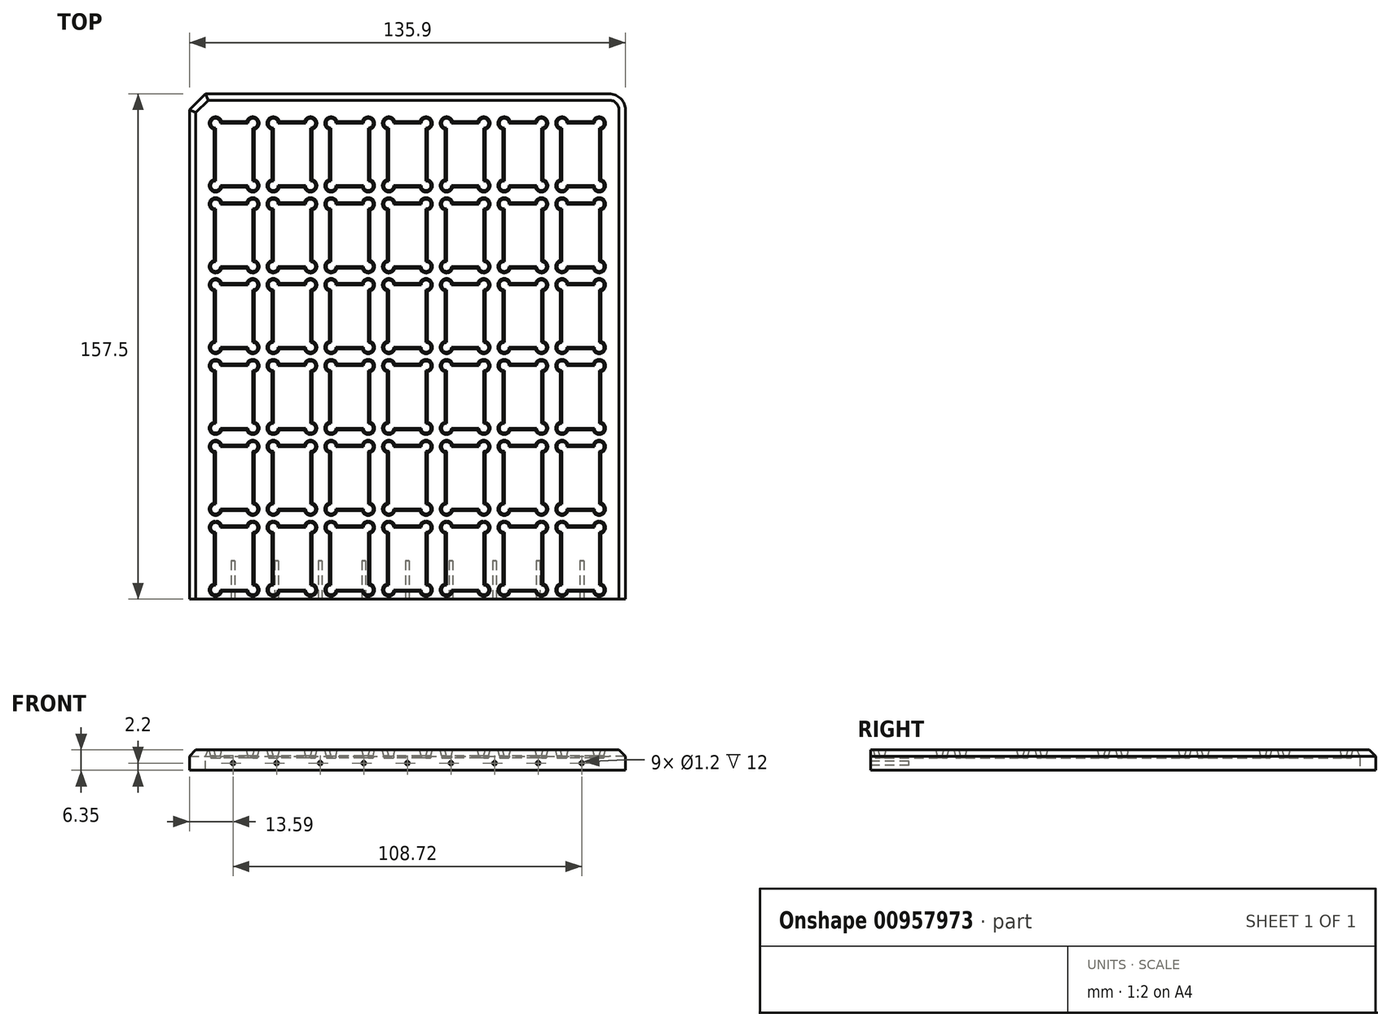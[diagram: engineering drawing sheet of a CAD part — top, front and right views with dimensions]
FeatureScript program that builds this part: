
annotation { "Feature Type Name" : "Feature", "Feature Type Description" : "" }
export const myFeature = defineFeature(function(context is Context, id is Id, definition is map)
    precondition{}
    {
        {
            var Q0;
            Q0=qCreatedBy(makeId("Top.planeOp"),FACE);
            var sketch = newSketch(context, id + "F0", { "sketchPlane" : qUnion([Q0])});
            skLineSegment(sketch, "E0.bottom", {"start": v(0, 0) * mm, "end": v(135.9, 0) * mm});
            skLineSegment(sketch, "E0.top", {"start": v(0, -157.5) * mm, "end": v(135.9, -157.5) * mm});
            skLineSegment(sketch, "E0.left", {"start": v(0, 0) * mm, "end": v(0, -157.5) * mm});
            skLineSegment(sketch, "E0.right", {"start": v(135.9, 0) * mm, "end": v(135.9, -157.5) * mm});
            skSolve(sketch);
        }
        {
            var Q0;
            Q0=makeQuery(id+"F0.imprint","IMPRINT",FACE,{"disambiguationData":[TD([[makeQuery(id+"F0.imprint","IMPRINT",EDGE,{"derivedFrom":sQuery(id+"F0.wireOp",EDGE,"E0.bottom")}),-1.0]])]});
            extrude(context, id + "F1", {"entities" : qUnion([Q0]), "depth" : 3.85 * mm, "offsetDistance" : 25 * mm});
        }
        {
            var Q0;
            Q0=makeQuery(id+"F1.opExtrude","SWEPT_EDGE",EDGE,{"disambiguationData":[OSD([sQuery(id+"F0.wireOp",EDGE,"E0.bottom"),sQuery(id+"F0.wireOp",EDGE,"E0.left")])]});
            chamfer(context, id + "F2", {"entities" : qUnion([Q0]), "chamferType" : ChamferType.OFFSET_ANGLE, "width" : 5 * mm, "oppositeDirection" : false, "angle" : 45 * degree, "tangentPropagation" : true});
        }
        {
            var Q0;
            {var subQ0=sQuery(id+"F0.wireOp",EDGE,"E0.right");var subQ1=sQuery(id+"F0.wireOp",EDGE,"E0.bottom");Q0=makeQuery(id+"F5.boolean.opBoolean","MERGE",EDGE,{"derivedFrom":[makeQuery(id+"F1.opExtrude","SWEPT_EDGE",EDGE,{"disambiguationData":[OSD([subQ1,subQ0])]}),makeQuery(id+"F5.opExtrude","SWEPT_EDGE",EDGE,{"disambiguationData":[OSD([subQ1,subQ0])]})]});}
            fillet(context, id + "F3", {"entities" : qUnion([Q0]), "radius" : 5 * mm, "tangentPropagation" : true, "allowEdgeOverflow" : false});
        }
        {
            var Q0;
            Q0=makeQuery(id+"F1.opExtrude","CAP_FACE",FACE,{"disambiguationData":[OSD([sQuery(id+"F0.wireOp",EDGE,"E0.bottom"),sQuery(id+"F0.wireOp",EDGE,"E0.top"),sQuery(id+"F0.wireOp",EDGE,"E0.left"),sQuery(id+"F0.wireOp",EDGE,"E0.right")])],"isStart":false});
            var sketch = newSketch(context, id + "F4", { "sketchPlane" : qUnion([Q0])});
            skLineSegment(sketch, "E1.bottom", {"start": v(19.75, -28.64) * mm, "end": v(8.15, -28.64) * mm});
            skLineSegment(sketch, "E1.top", {"start": v(19.75, -9.17) * mm, "end": v(8.15, -9.17) * mm});
            skLineSegment(sketch, "E1.left", {"start": v(19.75, -28.64) * mm, "end": v(19.75, -9.17) * mm});
            skLineSegment(sketch, "E1.right", {"start": v(8.15, -28.64) * mm, "end": v(8.15, -9.17) * mm});
            skPoint(sketch, "E1.middle", {"position": v(13.95, -18.9) * mm});
            skCircle(sketch, "E2", {"center": v(8.15, -9.17) * mm, "radius": 1.5 * mm});
            skCircle(sketch, "E3", {"center": v(19.75, -9.17) * mm, "radius": 1.5 * mm});
            skCircle(sketch, "E4", {"center": v(19.75, -28.64) * mm, "radius": 1.5 * mm});
            skCircle(sketch, "E5", {"center": v(8.15, -28.64) * mm, "radius": 1.5 * mm});
            skLineSegment(sketch, "E6.0.1.0", {"start": v(19.75, -53.84) * mm, "end": v(8.15, -53.84) * mm});
            skCircle(sketch, "E6.0.1.1", {"center": v(8.15, -53.84) * mm, "radius": 1.5 * mm});
            skLineSegment(sketch, "E6.0.1.2", {"start": v(8.15, -53.84) * mm, "end": v(8.15, -34.37) * mm});
            skCircle(sketch, "E6.0.1.3", {"center": v(8.15, -34.37) * mm, "radius": 1.5 * mm});
            skLineSegment(sketch, "E6.0.1.4", {"start": v(19.75, -34.37) * mm, "end": v(8.15, -34.37) * mm});
            skCircle(sketch, "E6.0.1.5", {"center": v(19.75, -34.37) * mm, "radius": 1.5 * mm});
            skLineSegment(sketch, "E6.0.1.6", {"start": v(19.75, -53.84) * mm, "end": v(19.75, -34.37) * mm});
            skCircle(sketch, "E6.0.1.7", {"center": v(19.75, -53.84) * mm, "radius": 1.5 * mm});
            skLineSegment(sketch, "E6.0.2.0", {"start": v(19.75, -79.04) * mm, "end": v(8.15, -79.04) * mm});
            skCircle(sketch, "E6.0.2.1", {"center": v(8.15, -79.04) * mm, "radius": 1.5 * mm});
            skLineSegment(sketch, "E6.0.2.2", {"start": v(8.15, -79.04) * mm, "end": v(8.15, -59.57) * mm});
            skCircle(sketch, "E6.0.2.3", {"center": v(8.15, -59.57) * mm, "radius": 1.5 * mm});
            skLineSegment(sketch, "E6.0.2.4", {"start": v(19.75, -59.57) * mm, "end": v(8.15, -59.57) * mm});
            skCircle(sketch, "E6.0.2.5", {"center": v(19.75, -59.57) * mm, "radius": 1.5 * mm});
            skLineSegment(sketch, "E6.0.2.6", {"start": v(19.75, -79.04) * mm, "end": v(19.75, -59.57) * mm});
            skCircle(sketch, "E6.0.2.7", {"center": v(19.75, -79.04) * mm, "radius": 1.5 * mm});
            skLineSegment(sketch, "E6.0.3.0", {"start": v(19.75, -104.24) * mm, "end": v(8.15, -104.24) * mm});
            skCircle(sketch, "E6.0.3.1", {"center": v(8.15, -104.24) * mm, "radius": 1.5 * mm});
            skLineSegment(sketch, "E6.0.3.2", {"start": v(8.15, -104.24) * mm, "end": v(8.15, -84.77) * mm});
            skCircle(sketch, "E6.0.3.3", {"center": v(8.15, -84.77) * mm, "radius": 1.5 * mm});
            skLineSegment(sketch, "E6.0.3.4", {"start": v(19.75, -84.77) * mm, "end": v(8.15, -84.77) * mm});
            skCircle(sketch, "E6.0.3.5", {"center": v(19.75, -84.77) * mm, "radius": 1.5 * mm});
            skLineSegment(sketch, "E6.0.3.6", {"start": v(19.75, -104.24) * mm, "end": v(19.75, -84.77) * mm});
            skCircle(sketch, "E6.0.3.7", {"center": v(19.75, -104.24) * mm, "radius": 1.5 * mm});
            skLineSegment(sketch, "E6.0.4.0", {"start": v(19.75, -129.44) * mm, "end": v(8.15, -129.44) * mm});
            skCircle(sketch, "E6.0.4.1", {"center": v(8.15, -129.44) * mm, "radius": 1.5 * mm});
            skLineSegment(sketch, "E6.0.4.2", {"start": v(8.15, -129.44) * mm, "end": v(8.15, -109.97) * mm});
            skCircle(sketch, "E6.0.4.3", {"center": v(8.15, -109.97) * mm, "radius": 1.5 * mm});
            skLineSegment(sketch, "E6.0.4.4", {"start": v(19.75, -109.97) * mm, "end": v(8.15, -109.97) * mm});
            skCircle(sketch, "E6.0.4.5", {"center": v(19.75, -109.97) * mm, "radius": 1.5 * mm});
            skLineSegment(sketch, "E6.0.4.6", {"start": v(19.75, -129.44) * mm, "end": v(19.75, -109.97) * mm});
            skCircle(sketch, "E6.0.4.7", {"center": v(19.75, -129.44) * mm, "radius": 1.5 * mm});
            skLineSegment(sketch, "E6.1.0.0", {"start": v(37.75, -28.64) * mm, "end": v(26.15, -28.64) * mm});
            skCircle(sketch, "E6.1.0.1", {"center": v(26.15, -28.64) * mm, "radius": 1.5 * mm});
            skLineSegment(sketch, "E6.1.0.2", {"start": v(26.15, -28.64) * mm, "end": v(26.15, -9.17) * mm});
            skCircle(sketch, "E6.1.0.3", {"center": v(26.15, -9.17) * mm, "radius": 1.5 * mm});
            skLineSegment(sketch, "E6.1.0.4", {"start": v(37.75, -9.17) * mm, "end": v(26.15, -9.17) * mm});
            skCircle(sketch, "E6.1.0.5", {"center": v(37.75, -9.17) * mm, "radius": 1.5 * mm});
            skLineSegment(sketch, "E6.1.0.6", {"start": v(37.75, -28.64) * mm, "end": v(37.75, -9.17) * mm});
            skCircle(sketch, "E6.1.0.7", {"center": v(37.75, -28.64) * mm, "radius": 1.5 * mm});
            skLineSegment(sketch, "E6.1.1.0", {"start": v(37.75, -53.84) * mm, "end": v(26.15, -53.84) * mm});
            skCircle(sketch, "E6.1.1.1", {"center": v(26.15, -53.84) * mm, "radius": 1.5 * mm});
            skLineSegment(sketch, "E6.1.1.2", {"start": v(26.15, -53.84) * mm, "end": v(26.15, -34.37) * mm});
            skCircle(sketch, "E6.1.1.3", {"center": v(26.15, -34.37) * mm, "radius": 1.5 * mm});
            skLineSegment(sketch, "E6.1.1.4", {"start": v(37.75, -34.37) * mm, "end": v(26.15, -34.37) * mm});
            skCircle(sketch, "E6.1.1.5", {"center": v(37.75, -34.37) * mm, "radius": 1.5 * mm});
            skLineSegment(sketch, "E6.1.1.6", {"start": v(37.75, -53.84) * mm, "end": v(37.75, -34.37) * mm});
            skCircle(sketch, "E6.1.1.7", {"center": v(37.75, -53.84) * mm, "radius": 1.5 * mm});
            skLineSegment(sketch, "E6.1.2.0", {"start": v(37.75, -79.04) * mm, "end": v(26.15, -79.04) * mm});
            skCircle(sketch, "E6.1.2.1", {"center": v(26.15, -79.04) * mm, "radius": 1.5 * mm});
            skLineSegment(sketch, "E6.1.2.2", {"start": v(26.15, -79.04) * mm, "end": v(26.15, -59.57) * mm});
            skCircle(sketch, "E6.1.2.3", {"center": v(26.15, -59.57) * mm, "radius": 1.5 * mm});
            skLineSegment(sketch, "E6.1.2.4", {"start": v(37.75, -59.57) * mm, "end": v(26.15, -59.57) * mm});
            skCircle(sketch, "E6.1.2.5", {"center": v(37.75, -59.57) * mm, "radius": 1.5 * mm});
            skLineSegment(sketch, "E6.1.2.6", {"start": v(37.75, -79.04) * mm, "end": v(37.75, -59.57) * mm});
            skCircle(sketch, "E6.1.2.7", {"center": v(37.75, -79.04) * mm, "radius": 1.5 * mm});
            skLineSegment(sketch, "E6.1.3.0", {"start": v(37.75, -104.24) * mm, "end": v(26.15, -104.24) * mm});
            skCircle(sketch, "E6.1.3.1", {"center": v(26.15, -104.24) * mm, "radius": 1.5 * mm});
            skLineSegment(sketch, "E6.1.3.2", {"start": v(26.15, -104.24) * mm, "end": v(26.15, -84.77) * mm});
            skCircle(sketch, "E6.1.3.3", {"center": v(26.15, -84.77) * mm, "radius": 1.5 * mm});
            skLineSegment(sketch, "E6.1.3.4", {"start": v(37.75, -84.77) * mm, "end": v(26.15, -84.77) * mm});
            skCircle(sketch, "E6.1.3.5", {"center": v(37.75, -84.77) * mm, "radius": 1.5 * mm});
            skLineSegment(sketch, "E6.1.3.6", {"start": v(37.75, -104.24) * mm, "end": v(37.75, -84.77) * mm});
            skCircle(sketch, "E6.1.3.7", {"center": v(37.75, -104.24) * mm, "radius": 1.5 * mm});
            skLineSegment(sketch, "E6.1.4.0", {"start": v(37.75, -129.44) * mm, "end": v(26.15, -129.44) * mm});
            skCircle(sketch, "E6.1.4.1", {"center": v(26.15, -129.44) * mm, "radius": 1.5 * mm});
            skLineSegment(sketch, "E6.1.4.2", {"start": v(26.15, -129.44) * mm, "end": v(26.15, -109.97) * mm});
            skCircle(sketch, "E6.1.4.3", {"center": v(26.15, -109.97) * mm, "radius": 1.5 * mm});
            skLineSegment(sketch, "E6.1.4.4", {"start": v(37.75, -109.97) * mm, "end": v(26.15, -109.97) * mm});
            skCircle(sketch, "E6.1.4.5", {"center": v(37.75, -109.97) * mm, "radius": 1.5 * mm});
            skLineSegment(sketch, "E6.1.4.6", {"start": v(37.75, -129.44) * mm, "end": v(37.75, -109.97) * mm});
            skCircle(sketch, "E6.1.4.7", {"center": v(37.75, -129.44) * mm, "radius": 1.5 * mm});
            skLineSegment(sketch, "E6.2.0.0", {"start": v(55.75, -28.64) * mm, "end": v(44.15, -28.64) * mm});
            skCircle(sketch, "E6.2.0.1", {"center": v(44.15, -28.64) * mm, "radius": 1.5 * mm});
            skLineSegment(sketch, "E6.2.0.2", {"start": v(44.15, -28.64) * mm, "end": v(44.15, -9.17) * mm});
            skCircle(sketch, "E6.2.0.3", {"center": v(44.15, -9.17) * mm, "radius": 1.5 * mm});
            skLineSegment(sketch, "E6.2.0.4", {"start": v(55.75, -9.17) * mm, "end": v(44.15, -9.17) * mm});
            skCircle(sketch, "E6.2.0.5", {"center": v(55.75, -9.17) * mm, "radius": 1.5 * mm});
            skLineSegment(sketch, "E6.2.0.6", {"start": v(55.75, -28.64) * mm, "end": v(55.75, -9.17) * mm});
            skCircle(sketch, "E6.2.0.7", {"center": v(55.75, -28.64) * mm, "radius": 1.5 * mm});
            skLineSegment(sketch, "E6.2.1.0", {"start": v(55.75, -53.84) * mm, "end": v(44.15, -53.84) * mm});
            skCircle(sketch, "E6.2.1.1", {"center": v(44.15, -53.84) * mm, "radius": 1.5 * mm});
            skLineSegment(sketch, "E6.2.1.2", {"start": v(44.15, -53.84) * mm, "end": v(44.15, -34.37) * mm});
            skCircle(sketch, "E6.2.1.3", {"center": v(44.15, -34.37) * mm, "radius": 1.5 * mm});
            skLineSegment(sketch, "E6.2.1.4", {"start": v(55.75, -34.37) * mm, "end": v(44.15, -34.37) * mm});
            skCircle(sketch, "E6.2.1.5", {"center": v(55.75, -34.37) * mm, "radius": 1.5 * mm});
            skLineSegment(sketch, "E6.2.1.6", {"start": v(55.75, -53.84) * mm, "end": v(55.75, -34.37) * mm});
            skCircle(sketch, "E6.2.1.7", {"center": v(55.75, -53.84) * mm, "radius": 1.5 * mm});
            skLineSegment(sketch, "E6.2.2.0", {"start": v(55.75, -79.04) * mm, "end": v(44.15, -79.04) * mm});
            skCircle(sketch, "E6.2.2.1", {"center": v(44.15, -79.04) * mm, "radius": 1.5 * mm});
            skLineSegment(sketch, "E6.2.2.2", {"start": v(44.15, -79.04) * mm, "end": v(44.15, -59.57) * mm});
            skCircle(sketch, "E6.2.2.3", {"center": v(44.15, -59.57) * mm, "radius": 1.5 * mm});
            skLineSegment(sketch, "E6.2.2.4", {"start": v(55.75, -59.57) * mm, "end": v(44.15, -59.57) * mm});
            skCircle(sketch, "E6.2.2.5", {"center": v(55.75, -59.57) * mm, "radius": 1.5 * mm});
            skLineSegment(sketch, "E6.2.2.6", {"start": v(55.75, -79.04) * mm, "end": v(55.75, -59.57) * mm});
            skCircle(sketch, "E6.2.2.7", {"center": v(55.75, -79.04) * mm, "radius": 1.5 * mm});
            skLineSegment(sketch, "E6.2.3.0", {"start": v(55.75, -104.24) * mm, "end": v(44.15, -104.24) * mm});
            skCircle(sketch, "E6.2.3.1", {"center": v(44.15, -104.24) * mm, "radius": 1.5 * mm});
            skLineSegment(sketch, "E6.2.3.2", {"start": v(44.15, -104.24) * mm, "end": v(44.15, -84.77) * mm});
            skCircle(sketch, "E6.2.3.3", {"center": v(44.15, -84.77) * mm, "radius": 1.5 * mm});
            skLineSegment(sketch, "E6.2.3.4", {"start": v(55.75, -84.77) * mm, "end": v(44.15, -84.77) * mm});
            skCircle(sketch, "E6.2.3.5", {"center": v(55.75, -84.77) * mm, "radius": 1.5 * mm});
            skLineSegment(sketch, "E6.2.3.6", {"start": v(55.75, -104.24) * mm, "end": v(55.75, -84.77) * mm});
            skCircle(sketch, "E6.2.3.7", {"center": v(55.75, -104.24) * mm, "radius": 1.5 * mm});
            skLineSegment(sketch, "E6.2.4.0", {"start": v(55.75, -129.44) * mm, "end": v(44.15, -129.44) * mm});
            skCircle(sketch, "E6.2.4.1", {"center": v(44.15, -129.44) * mm, "radius": 1.5 * mm});
            skLineSegment(sketch, "E6.2.4.2", {"start": v(44.15, -129.44) * mm, "end": v(44.15, -109.97) * mm});
            skCircle(sketch, "E6.2.4.3", {"center": v(44.15, -109.97) * mm, "radius": 1.5 * mm});
            skLineSegment(sketch, "E6.2.4.4", {"start": v(55.75, -109.97) * mm, "end": v(44.15, -109.97) * mm});
            skCircle(sketch, "E6.2.4.5", {"center": v(55.75, -109.97) * mm, "radius": 1.5 * mm});
            skLineSegment(sketch, "E6.2.4.6", {"start": v(55.75, -129.44) * mm, "end": v(55.75, -109.97) * mm});
            skCircle(sketch, "E6.2.4.7", {"center": v(55.75, -129.44) * mm, "radius": 1.5 * mm});
            skLineSegment(sketch, "E6.3.0.0", {"start": v(73.75, -28.64) * mm, "end": v(62.15, -28.64) * mm});
            skCircle(sketch, "E6.3.0.1", {"center": v(62.15, -28.64) * mm, "radius": 1.5 * mm});
            skLineSegment(sketch, "E6.3.0.2", {"start": v(62.15, -28.64) * mm, "end": v(62.15, -9.17) * mm});
            skCircle(sketch, "E6.3.0.3", {"center": v(62.15, -9.17) * mm, "radius": 1.5 * mm});
            skLineSegment(sketch, "E6.3.0.4", {"start": v(73.75, -9.17) * mm, "end": v(62.15, -9.17) * mm});
            skCircle(sketch, "E6.3.0.5", {"center": v(73.75, -9.17) * mm, "radius": 1.5 * mm});
            skLineSegment(sketch, "E6.3.0.6", {"start": v(73.75, -28.64) * mm, "end": v(73.75, -9.17) * mm});
            skCircle(sketch, "E6.3.0.7", {"center": v(73.75, -28.64) * mm, "radius": 1.5 * mm});
            skLineSegment(sketch, "E6.3.1.0", {"start": v(73.75, -53.84) * mm, "end": v(62.15, -53.84) * mm});
            skCircle(sketch, "E6.3.1.1", {"center": v(62.15, -53.84) * mm, "radius": 1.5 * mm});
            skLineSegment(sketch, "E6.3.1.2", {"start": v(62.15, -53.84) * mm, "end": v(62.15, -34.37) * mm});
            skCircle(sketch, "E6.3.1.3", {"center": v(62.15, -34.37) * mm, "radius": 1.5 * mm});
            skLineSegment(sketch, "E6.3.1.4", {"start": v(73.75, -34.37) * mm, "end": v(62.15, -34.37) * mm});
            skCircle(sketch, "E6.3.1.5", {"center": v(73.75, -34.37) * mm, "radius": 1.5 * mm});
            skLineSegment(sketch, "E6.3.1.6", {"start": v(73.75, -53.84) * mm, "end": v(73.75, -34.37) * mm});
            skCircle(sketch, "E6.3.1.7", {"center": v(73.75, -53.84) * mm, "radius": 1.5 * mm});
            skLineSegment(sketch, "E6.3.2.0", {"start": v(73.75, -79.04) * mm, "end": v(62.15, -79.04) * mm});
            skCircle(sketch, "E6.3.2.1", {"center": v(62.15, -79.04) * mm, "radius": 1.5 * mm});
            skLineSegment(sketch, "E6.3.2.2", {"start": v(62.15, -79.04) * mm, "end": v(62.15, -59.57) * mm});
            skCircle(sketch, "E6.3.2.3", {"center": v(62.15, -59.57) * mm, "radius": 1.5 * mm});
            skLineSegment(sketch, "E6.3.2.4", {"start": v(73.75, -59.57) * mm, "end": v(62.15, -59.57) * mm});
            skCircle(sketch, "E6.3.2.5", {"center": v(73.75, -59.57) * mm, "radius": 1.5 * mm});
            skLineSegment(sketch, "E6.3.2.6", {"start": v(73.75, -79.04) * mm, "end": v(73.75, -59.57) * mm});
            skCircle(sketch, "E6.3.2.7", {"center": v(73.75, -79.04) * mm, "radius": 1.5 * mm});
            skLineSegment(sketch, "E6.3.3.0", {"start": v(73.75, -104.24) * mm, "end": v(62.15, -104.24) * mm});
            skCircle(sketch, "E6.3.3.1", {"center": v(62.15, -104.24) * mm, "radius": 1.5 * mm});
            skLineSegment(sketch, "E6.3.3.2", {"start": v(62.15, -104.24) * mm, "end": v(62.15, -84.77) * mm});
            skCircle(sketch, "E6.3.3.3", {"center": v(62.15, -84.77) * mm, "radius": 1.5 * mm});
            skLineSegment(sketch, "E6.3.3.4", {"start": v(73.75, -84.77) * mm, "end": v(62.15, -84.77) * mm});
            skCircle(sketch, "E6.3.3.5", {"center": v(73.75, -84.77) * mm, "radius": 1.5 * mm});
            skLineSegment(sketch, "E6.3.3.6", {"start": v(73.75, -104.24) * mm, "end": v(73.75, -84.77) * mm});
            skCircle(sketch, "E6.3.3.7", {"center": v(73.75, -104.24) * mm, "radius": 1.5 * mm});
            skLineSegment(sketch, "E6.3.4.0", {"start": v(73.75, -129.44) * mm, "end": v(62.15, -129.44) * mm});
            skCircle(sketch, "E6.3.4.1", {"center": v(62.15, -129.44) * mm, "radius": 1.5 * mm});
            skLineSegment(sketch, "E6.3.4.2", {"start": v(62.15, -129.44) * mm, "end": v(62.15, -109.97) * mm});
            skCircle(sketch, "E6.3.4.3", {"center": v(62.15, -109.97) * mm, "radius": 1.5 * mm});
            skLineSegment(sketch, "E6.3.4.4", {"start": v(73.75, -109.97) * mm, "end": v(62.15, -109.97) * mm});
            skCircle(sketch, "E6.3.4.5", {"center": v(73.75, -109.97) * mm, "radius": 1.5 * mm});
            skLineSegment(sketch, "E6.3.4.6", {"start": v(73.75, -129.44) * mm, "end": v(73.75, -109.97) * mm});
            skCircle(sketch, "E6.3.4.7", {"center": v(73.75, -129.44) * mm, "radius": 1.5 * mm});
            skLineSegment(sketch, "E6.4.0.0", {"start": v(91.75, -28.64) * mm, "end": v(80.15, -28.64) * mm});
            skCircle(sketch, "E6.4.0.1", {"center": v(80.15, -28.64) * mm, "radius": 1.5 * mm});
            skLineSegment(sketch, "E6.4.0.2", {"start": v(80.15, -28.64) * mm, "end": v(80.15, -9.17) * mm});
            skCircle(sketch, "E6.4.0.3", {"center": v(80.15, -9.17) * mm, "radius": 1.5 * mm});
            skLineSegment(sketch, "E6.4.0.4", {"start": v(91.75, -9.17) * mm, "end": v(80.15, -9.17) * mm});
            skCircle(sketch, "E6.4.0.5", {"center": v(91.75, -9.17) * mm, "radius": 1.5 * mm});
            skLineSegment(sketch, "E6.4.0.6", {"start": v(91.75, -28.64) * mm, "end": v(91.75, -9.17) * mm});
            skCircle(sketch, "E6.4.0.7", {"center": v(91.75, -28.64) * mm, "radius": 1.5 * mm});
            skLineSegment(sketch, "E6.4.1.0", {"start": v(91.75, -53.84) * mm, "end": v(80.15, -53.84) * mm});
            skCircle(sketch, "E6.4.1.1", {"center": v(80.15, -53.84) * mm, "radius": 1.5 * mm});
            skLineSegment(sketch, "E6.4.1.2", {"start": v(80.15, -53.84) * mm, "end": v(80.15, -34.37) * mm});
            skCircle(sketch, "E6.4.1.3", {"center": v(80.15, -34.37) * mm, "radius": 1.5 * mm});
            skLineSegment(sketch, "E6.4.1.4", {"start": v(91.75, -34.37) * mm, "end": v(80.15, -34.37) * mm});
            skCircle(sketch, "E6.4.1.5", {"center": v(91.75, -34.37) * mm, "radius": 1.5 * mm});
            skLineSegment(sketch, "E6.4.1.6", {"start": v(91.75, -53.84) * mm, "end": v(91.75, -34.37) * mm});
            skCircle(sketch, "E6.4.1.7", {"center": v(91.75, -53.84) * mm, "radius": 1.5 * mm});
            skLineSegment(sketch, "E6.4.2.0", {"start": v(91.75, -79.04) * mm, "end": v(80.15, -79.04) * mm});
            skCircle(sketch, "E6.4.2.1", {"center": v(80.15, -79.04) * mm, "radius": 1.5 * mm});
            skLineSegment(sketch, "E6.4.2.2", {"start": v(80.15, -79.04) * mm, "end": v(80.15, -59.57) * mm});
            skCircle(sketch, "E6.4.2.3", {"center": v(80.15, -59.57) * mm, "radius": 1.5 * mm});
            skLineSegment(sketch, "E6.4.2.4", {"start": v(91.75, -59.57) * mm, "end": v(80.15, -59.57) * mm});
            skCircle(sketch, "E6.4.2.5", {"center": v(91.75, -59.57) * mm, "radius": 1.5 * mm});
            skLineSegment(sketch, "E6.4.2.6", {"start": v(91.75, -79.04) * mm, "end": v(91.75, -59.57) * mm});
            skCircle(sketch, "E6.4.2.7", {"center": v(91.75, -79.04) * mm, "radius": 1.5 * mm});
            skLineSegment(sketch, "E6.4.3.0", {"start": v(91.75, -104.24) * mm, "end": v(80.15, -104.24) * mm});
            skCircle(sketch, "E6.4.3.1", {"center": v(80.15, -104.24) * mm, "radius": 1.5 * mm});
            skLineSegment(sketch, "E6.4.3.2", {"start": v(80.15, -104.24) * mm, "end": v(80.15, -84.77) * mm});
            skCircle(sketch, "E6.4.3.3", {"center": v(80.15, -84.77) * mm, "radius": 1.5 * mm});
            skLineSegment(sketch, "E6.4.3.4", {"start": v(91.75, -84.77) * mm, "end": v(80.15, -84.77) * mm});
            skCircle(sketch, "E6.4.3.5", {"center": v(91.75, -84.77) * mm, "radius": 1.5 * mm});
            skLineSegment(sketch, "E6.4.3.6", {"start": v(91.75, -104.24) * mm, "end": v(91.75, -84.77) * mm});
            skCircle(sketch, "E6.4.3.7", {"center": v(91.75, -104.24) * mm, "radius": 1.5 * mm});
            skLineSegment(sketch, "E6.4.4.0", {"start": v(91.75, -129.44) * mm, "end": v(80.15, -129.44) * mm});
            skCircle(sketch, "E6.4.4.1", {"center": v(80.15, -129.44) * mm, "radius": 1.5 * mm});
            skLineSegment(sketch, "E6.4.4.2", {"start": v(80.15, -129.44) * mm, "end": v(80.15, -109.97) * mm});
            skCircle(sketch, "E6.4.4.3", {"center": v(80.15, -109.97) * mm, "radius": 1.5 * mm});
            skLineSegment(sketch, "E6.4.4.4", {"start": v(91.75, -109.97) * mm, "end": v(80.15, -109.97) * mm});
            skCircle(sketch, "E6.4.4.5", {"center": v(91.75, -109.97) * mm, "radius": 1.5 * mm});
            skLineSegment(sketch, "E6.4.4.6", {"start": v(91.75, -129.44) * mm, "end": v(91.75, -109.97) * mm});
            skCircle(sketch, "E6.4.4.7", {"center": v(91.75, -129.44) * mm, "radius": 1.5 * mm});
            skLineSegment(sketch, "E6.direction1", {"start": v(8.15, -28.64) * mm, "end": v(26.15, -28.64) * mm, "construction": true});
            skLineSegment(sketch, "E6.direction2", {"start": v(8.15, -28.64) * mm, "end": v(8.15, -53.84) * mm, "construction": true});
            skLineSegment(sketch, "E7.0.5.0", {"start": v(109.75, -28.64) * mm, "end": v(98.15, -28.64) * mm});
            skCircle(sketch, "E7.3.5.0", {"center": v(98.15, -28.64) * mm, "radius": 1.5 * mm});
            skLineSegment(sketch, "E7.5.5.0", {"start": v(98.15, -28.64) * mm, "end": v(98.15, -9.17) * mm});
            skCircle(sketch, "E7.8.5.0", {"center": v(98.15, -9.17) * mm, "radius": 1.5 * mm});
            skLineSegment(sketch, "E7.10.5.0", {"start": v(109.75, -9.17) * mm, "end": v(98.15, -9.17) * mm});
            skCircle(sketch, "E7.13.5.0", {"center": v(109.75, -9.17) * mm, "radius": 1.5 * mm});
            skLineSegment(sketch, "E7.15.5.0", {"start": v(109.75, -28.64) * mm, "end": v(109.75, -9.17) * mm});
            skCircle(sketch, "E7.18.5.0", {"center": v(109.75, -28.64) * mm, "radius": 1.5 * mm});
            skLineSegment(sketch, "E7.0.5.1", {"start": v(109.75, -53.84) * mm, "end": v(98.15, -53.84) * mm});
            skCircle(sketch, "E7.3.5.1", {"center": v(98.15, -53.84) * mm, "radius": 1.5 * mm});
            skLineSegment(sketch, "E7.5.5.1", {"start": v(98.15, -53.84) * mm, "end": v(98.15, -34.37) * mm});
            skCircle(sketch, "E7.8.5.1", {"center": v(98.15, -34.37) * mm, "radius": 1.5 * mm});
            skLineSegment(sketch, "E7.10.5.1", {"start": v(109.75, -34.37) * mm, "end": v(98.15, -34.37) * mm});
            skCircle(sketch, "E7.13.5.1", {"center": v(109.75, -34.37) * mm, "radius": 1.5 * mm});
            skLineSegment(sketch, "E7.15.5.1", {"start": v(109.75, -53.84) * mm, "end": v(109.75, -34.37) * mm});
            skCircle(sketch, "E7.18.5.1", {"center": v(109.75, -53.84) * mm, "radius": 1.5 * mm});
            skLineSegment(sketch, "E7.0.5.2", {"start": v(109.75, -79.04) * mm, "end": v(98.15, -79.04) * mm});
            skCircle(sketch, "E7.3.5.2", {"center": v(98.15, -79.04) * mm, "radius": 1.5 * mm});
            skLineSegment(sketch, "E7.5.5.2", {"start": v(98.15, -79.04) * mm, "end": v(98.15, -59.57) * mm});
            skCircle(sketch, "E7.8.5.2", {"center": v(98.15, -59.57) * mm, "radius": 1.5 * mm});
            skLineSegment(sketch, "E7.10.5.2", {"start": v(109.75, -59.57) * mm, "end": v(98.15, -59.57) * mm});
            skCircle(sketch, "E7.13.5.2", {"center": v(109.75, -59.57) * mm, "radius": 1.5 * mm});
            skLineSegment(sketch, "E7.15.5.2", {"start": v(109.75, -79.04) * mm, "end": v(109.75, -59.57) * mm});
            skCircle(sketch, "E7.18.5.2", {"center": v(109.75, -79.04) * mm, "radius": 1.5 * mm});
            skLineSegment(sketch, "E7.0.5.3", {"start": v(109.75, -104.24) * mm, "end": v(98.15, -104.24) * mm});
            skCircle(sketch, "E7.3.5.3", {"center": v(98.15, -104.24) * mm, "radius": 1.5 * mm});
            skLineSegment(sketch, "E7.5.5.3", {"start": v(98.15, -104.24) * mm, "end": v(98.15, -84.77) * mm});
            skCircle(sketch, "E7.8.5.3", {"center": v(98.15, -84.77) * mm, "radius": 1.5 * mm});
            skLineSegment(sketch, "E7.10.5.3", {"start": v(109.75, -84.77) * mm, "end": v(98.15, -84.77) * mm});
            skCircle(sketch, "E7.13.5.3", {"center": v(109.75, -84.77) * mm, "radius": 1.5 * mm});
            skLineSegment(sketch, "E7.15.5.3", {"start": v(109.75, -104.24) * mm, "end": v(109.75, -84.77) * mm});
            skCircle(sketch, "E7.18.5.3", {"center": v(109.75, -104.24) * mm, "radius": 1.5 * mm});
            skLineSegment(sketch, "E7.0.5.4", {"start": v(109.75, -129.44) * mm, "end": v(98.15, -129.44) * mm});
            skCircle(sketch, "E7.3.5.4", {"center": v(98.15, -129.44) * mm, "radius": 1.5 * mm});
            skLineSegment(sketch, "E7.5.5.4", {"start": v(98.15, -129.44) * mm, "end": v(98.15, -109.97) * mm});
            skCircle(sketch, "E7.8.5.4", {"center": v(98.15, -109.97) * mm, "radius": 1.5 * mm});
            skLineSegment(sketch, "E7.10.5.4", {"start": v(109.75, -109.97) * mm, "end": v(98.15, -109.97) * mm});
            skCircle(sketch, "E7.13.5.4", {"center": v(109.75, -109.97) * mm, "radius": 1.5 * mm});
            skLineSegment(sketch, "E7.15.5.4", {"start": v(109.75, -129.44) * mm, "end": v(109.75, -109.97) * mm});
            skCircle(sketch, "E7.18.5.4", {"center": v(109.75, -129.44) * mm, "radius": 1.5 * mm});
            skLineSegment(sketch, "E7.0.6.0", {"start": v(127.75, -28.64) * mm, "end": v(116.15, -28.64) * mm});
            skCircle(sketch, "E7.3.6.0", {"center": v(116.15, -28.64) * mm, "radius": 1.5 * mm});
            skLineSegment(sketch, "E7.5.6.0", {"start": v(116.15, -28.64) * mm, "end": v(116.15, -9.17) * mm});
            skCircle(sketch, "E7.8.6.0", {"center": v(116.15, -9.17) * mm, "radius": 1.5 * mm});
            skLineSegment(sketch, "E7.10.6.0", {"start": v(127.75, -9.17) * mm, "end": v(116.15, -9.17) * mm});
            skCircle(sketch, "E7.13.6.0", {"center": v(127.75, -9.17) * mm, "radius": 1.5 * mm});
            skLineSegment(sketch, "E7.15.6.0", {"start": v(127.75, -28.64) * mm, "end": v(127.75, -9.17) * mm});
            skCircle(sketch, "E7.18.6.0", {"center": v(127.75, -28.64) * mm, "radius": 1.5 * mm});
            skLineSegment(sketch, "E7.0.6.1", {"start": v(127.75, -53.84) * mm, "end": v(116.15, -53.84) * mm});
            skCircle(sketch, "E7.3.6.1", {"center": v(116.15, -53.84) * mm, "radius": 1.5 * mm});
            skLineSegment(sketch, "E7.5.6.1", {"start": v(116.15, -53.84) * mm, "end": v(116.15, -34.37) * mm});
            skCircle(sketch, "E7.8.6.1", {"center": v(116.15, -34.37) * mm, "radius": 1.5 * mm});
            skLineSegment(sketch, "E7.10.6.1", {"start": v(127.75, -34.37) * mm, "end": v(116.15, -34.37) * mm});
            skCircle(sketch, "E7.13.6.1", {"center": v(127.75, -34.37) * mm, "radius": 1.5 * mm});
            skLineSegment(sketch, "E7.15.6.1", {"start": v(127.75, -53.84) * mm, "end": v(127.75, -34.37) * mm});
            skCircle(sketch, "E7.18.6.1", {"center": v(127.75, -53.84) * mm, "radius": 1.5 * mm});
            skLineSegment(sketch, "E7.0.6.2", {"start": v(127.75, -79.04) * mm, "end": v(116.15, -79.04) * mm});
            skCircle(sketch, "E7.3.6.2", {"center": v(116.15, -79.04) * mm, "radius": 1.5 * mm});
            skLineSegment(sketch, "E7.5.6.2", {"start": v(116.15, -79.04) * mm, "end": v(116.15, -59.57) * mm});
            skCircle(sketch, "E7.8.6.2", {"center": v(116.15, -59.57) * mm, "radius": 1.5 * mm});
            skLineSegment(sketch, "E7.10.6.2", {"start": v(127.75, -59.57) * mm, "end": v(116.15, -59.57) * mm});
            skCircle(sketch, "E7.13.6.2", {"center": v(127.75, -59.57) * mm, "radius": 1.5 * mm});
            skLineSegment(sketch, "E7.15.6.2", {"start": v(127.75, -79.04) * mm, "end": v(127.75, -59.57) * mm});
            skCircle(sketch, "E7.18.6.2", {"center": v(127.75, -79.04) * mm, "radius": 1.5 * mm});
            skLineSegment(sketch, "E7.0.6.3", {"start": v(127.75, -104.24) * mm, "end": v(116.15, -104.24) * mm});
            skCircle(sketch, "E7.3.6.3", {"center": v(116.15, -104.24) * mm, "radius": 1.5 * mm});
            skLineSegment(sketch, "E7.5.6.3", {"start": v(116.15, -104.24) * mm, "end": v(116.15, -84.77) * mm});
            skCircle(sketch, "E7.8.6.3", {"center": v(116.15, -84.77) * mm, "radius": 1.5 * mm});
            skLineSegment(sketch, "E7.10.6.3", {"start": v(127.75, -84.77) * mm, "end": v(116.15, -84.77) * mm});
            skCircle(sketch, "E7.13.6.3", {"center": v(127.75, -84.77) * mm, "radius": 1.5 * mm});
            skLineSegment(sketch, "E7.15.6.3", {"start": v(127.75, -104.24) * mm, "end": v(127.75, -84.77) * mm});
            skCircle(sketch, "E7.18.6.3", {"center": v(127.75, -104.24) * mm, "radius": 1.5 * mm});
            skLineSegment(sketch, "E7.0.6.4", {"start": v(127.75, -129.44) * mm, "end": v(116.15, -129.44) * mm});
            skCircle(sketch, "E7.3.6.4", {"center": v(116.15, -129.44) * mm, "radius": 1.5 * mm});
            skLineSegment(sketch, "E7.5.6.4", {"start": v(116.15, -129.44) * mm, "end": v(116.15, -109.97) * mm});
            skCircle(sketch, "E7.8.6.4", {"center": v(116.15, -109.97) * mm, "radius": 1.5 * mm});
            skLineSegment(sketch, "E7.10.6.4", {"start": v(127.75, -109.97) * mm, "end": v(116.15, -109.97) * mm});
            skCircle(sketch, "E7.13.6.4", {"center": v(127.75, -109.97) * mm, "radius": 1.5 * mm});
            skLineSegment(sketch, "E7.15.6.4", {"start": v(127.75, -129.44) * mm, "end": v(127.75, -109.97) * mm});
            skCircle(sketch, "E7.18.6.4", {"center": v(127.75, -129.44) * mm, "radius": 1.5 * mm});
            skLineSegment(sketch, "E8.0.0.5", {"start": v(19.75, -154.64) * mm, "end": v(8.15, -154.64) * mm});
            skCircle(sketch, "E8.3.0.5", {"center": v(8.15, -154.64) * mm, "radius": 1.5 * mm});
            skLineSegment(sketch, "E8.5.0.5", {"start": v(8.15, -154.64) * mm, "end": v(8.15, -135.17) * mm});
            skCircle(sketch, "E8.8.0.5", {"center": v(8.15, -135.17) * mm, "radius": 1.5 * mm});
            skLineSegment(sketch, "E8.10.0.5", {"start": v(19.75, -135.17) * mm, "end": v(8.15, -135.17) * mm});
            skCircle(sketch, "E8.13.0.5", {"center": v(19.75, -135.17) * mm, "radius": 1.5 * mm});
            skLineSegment(sketch, "E8.15.0.5", {"start": v(19.75, -154.64) * mm, "end": v(19.75, -135.17) * mm});
            skCircle(sketch, "E8.18.0.5", {"center": v(19.75, -154.64) * mm, "radius": 1.5 * mm});
            skLineSegment(sketch, "E8.0.1.5", {"start": v(37.75, -154.64) * mm, "end": v(26.15, -154.64) * mm});
            skCircle(sketch, "E8.3.1.5", {"center": v(26.15, -154.64) * mm, "radius": 1.5 * mm});
            skLineSegment(sketch, "E8.5.1.5", {"start": v(26.15, -154.64) * mm, "end": v(26.15, -135.17) * mm});
            skCircle(sketch, "E8.8.1.5", {"center": v(26.15, -135.17) * mm, "radius": 1.5 * mm});
            skLineSegment(sketch, "E8.10.1.5", {"start": v(37.75, -135.17) * mm, "end": v(26.15, -135.17) * mm});
            skCircle(sketch, "E8.13.1.5", {"center": v(37.75, -135.17) * mm, "radius": 1.5 * mm});
            skLineSegment(sketch, "E8.15.1.5", {"start": v(37.75, -154.64) * mm, "end": v(37.75, -135.17) * mm});
            skCircle(sketch, "E8.18.1.5", {"center": v(37.75, -154.64) * mm, "radius": 1.5 * mm});
            skLineSegment(sketch, "E8.0.2.5", {"start": v(55.75, -154.64) * mm, "end": v(44.15, -154.64) * mm});
            skCircle(sketch, "E8.3.2.5", {"center": v(44.15, -154.64) * mm, "radius": 1.5 * mm});
            skLineSegment(sketch, "E8.5.2.5", {"start": v(44.15, -154.64) * mm, "end": v(44.15, -135.17) * mm});
            skCircle(sketch, "E8.8.2.5", {"center": v(44.15, -135.17) * mm, "radius": 1.5 * mm});
            skLineSegment(sketch, "E8.10.2.5", {"start": v(55.75, -135.17) * mm, "end": v(44.15, -135.17) * mm});
            skCircle(sketch, "E8.13.2.5", {"center": v(55.75, -135.17) * mm, "radius": 1.5 * mm});
            skLineSegment(sketch, "E8.15.2.5", {"start": v(55.75, -154.64) * mm, "end": v(55.75, -135.17) * mm});
            skCircle(sketch, "E8.18.2.5", {"center": v(55.75, -154.64) * mm, "radius": 1.5 * mm});
            skLineSegment(sketch, "E8.0.3.5", {"start": v(73.75, -154.64) * mm, "end": v(62.15, -154.64) * mm});
            skCircle(sketch, "E8.3.3.5", {"center": v(62.15, -154.64) * mm, "radius": 1.5 * mm});
            skLineSegment(sketch, "E8.5.3.5", {"start": v(62.15, -154.64) * mm, "end": v(62.15, -135.17) * mm});
            skCircle(sketch, "E8.8.3.5", {"center": v(62.15, -135.17) * mm, "radius": 1.5 * mm});
            skLineSegment(sketch, "E8.10.3.5", {"start": v(73.75, -135.17) * mm, "end": v(62.15, -135.17) * mm});
            skCircle(sketch, "E8.13.3.5", {"center": v(73.75, -135.17) * mm, "radius": 1.5 * mm});
            skLineSegment(sketch, "E8.15.3.5", {"start": v(73.75, -154.64) * mm, "end": v(73.75, -135.17) * mm});
            skCircle(sketch, "E8.18.3.5", {"center": v(73.75, -154.64) * mm, "radius": 1.5 * mm});
            skLineSegment(sketch, "E8.0.4.5", {"start": v(91.75, -154.64) * mm, "end": v(80.15, -154.64) * mm});
            skCircle(sketch, "E8.3.4.5", {"center": v(80.15, -154.64) * mm, "radius": 1.5 * mm});
            skLineSegment(sketch, "E8.5.4.5", {"start": v(80.15, -154.64) * mm, "end": v(80.15, -135.17) * mm});
            skCircle(sketch, "E8.8.4.5", {"center": v(80.15, -135.17) * mm, "radius": 1.5 * mm});
            skLineSegment(sketch, "E8.10.4.5", {"start": v(91.75, -135.17) * mm, "end": v(80.15, -135.17) * mm});
            skCircle(sketch, "E8.13.4.5", {"center": v(91.75, -135.17) * mm, "radius": 1.5 * mm});
            skLineSegment(sketch, "E8.15.4.5", {"start": v(91.75, -154.64) * mm, "end": v(91.75, -135.17) * mm});
            skCircle(sketch, "E8.18.4.5", {"center": v(91.75, -154.64) * mm, "radius": 1.5 * mm});
            skLineSegment(sketch, "E8.0.5.5", {"start": v(109.75, -154.64) * mm, "end": v(98.15, -154.64) * mm});
            skCircle(sketch, "E8.3.5.5", {"center": v(98.15, -154.64) * mm, "radius": 1.5 * mm});
            skLineSegment(sketch, "E8.5.5.5", {"start": v(98.15, -154.64) * mm, "end": v(98.15, -135.17) * mm});
            skCircle(sketch, "E8.8.5.5", {"center": v(98.15, -135.17) * mm, "radius": 1.5 * mm});
            skLineSegment(sketch, "E8.10.5.5", {"start": v(109.75, -135.17) * mm, "end": v(98.15, -135.17) * mm});
            skCircle(sketch, "E8.13.5.5", {"center": v(109.75, -135.17) * mm, "radius": 1.5 * mm});
            skLineSegment(sketch, "E8.15.5.5", {"start": v(109.75, -154.64) * mm, "end": v(109.75, -135.17) * mm});
            skCircle(sketch, "E8.18.5.5", {"center": v(109.75, -154.64) * mm, "radius": 1.5 * mm});
            skLineSegment(sketch, "E8.0.6.5", {"start": v(127.75, -154.64) * mm, "end": v(116.15, -154.64) * mm});
            skCircle(sketch, "E8.3.6.5", {"center": v(116.15, -154.64) * mm, "radius": 1.5 * mm});
            skLineSegment(sketch, "E8.5.6.5", {"start": v(116.15, -154.64) * mm, "end": v(116.15, -135.17) * mm});
            skCircle(sketch, "E8.8.6.5", {"center": v(116.15, -135.17) * mm, "radius": 1.5 * mm});
            skLineSegment(sketch, "E8.10.6.5", {"start": v(127.75, -135.17) * mm, "end": v(116.15, -135.17) * mm});
            skCircle(sketch, "E8.13.6.5", {"center": v(127.75, -135.17) * mm, "radius": 1.5 * mm});
            skLineSegment(sketch, "E8.15.6.5", {"start": v(127.75, -154.64) * mm, "end": v(127.75, -135.17) * mm});
            skCircle(sketch, "E8.18.6.5", {"center": v(127.75, -154.64) * mm, "radius": 1.5 * mm});
            skSolve(sketch);
        }
        {
            var Q0;
            {var subQ603=sQuery(id+"F0.wireOp",EDGE,"E0.top");Q0=makeQuery(id+"F4.imprint","IMPRINT",FACE,{"disambiguationData":[TD([[makeQuery(id+"F4.imprint","IMPRINT",EDGE,{"derivedFrom":makeQuery(id+"F1.opExtrude","CAP_EDGE",EDGE,{"disambiguationData":[OSD([subQ603])],"isStart":false})}),1.0]])]});}
            extrude(context, id + "F5", {"entities" : qUnion([Q0]), "operationType" : NewBodyOperationType.ADD, "depth" : 2.5 * mm, "offsetDistance" : 25 * mm});
        }
        {
            var Q0;
            {var subQ0=sQuery(id+"F0.wireOp",EDGE,"E0.top");Q0=makeQuery(id+"F5.boolean.opBoolean","MERGE",FACE,{"derivedFrom":[makeQuery(id+"F1.opExtrude","SWEPT_FACE",FACE,{"disambiguationData":[OSD([subQ0])]}),makeQuery(id+"F5.opExtrude","SWEPT_FACE",FACE,{"disambiguationData":[OSD([subQ0])]})]});}
            var sketch = newSketch(context, id + "F6", { "sketchPlane" : qUnion([Q0])});
            skCircle(sketch, "E9", {"center": v(13.6, 2.2) * mm, "radius": 0.6 * mm});
            skCircle(sketch, "E10.1.0.0", {"center": v(27.18, 2.2) * mm, "radius": 0.6 * mm});
            skCircle(sketch, "E10.2.0.0", {"center": v(40.77, 2.2) * mm, "radius": 0.6 * mm});
            skCircle(sketch, "E10.3.0.0", {"center": v(54.36, 2.2) * mm, "radius": 0.6 * mm});
            skCircle(sketch, "E10.4.0.0", {"center": v(67.95, 2.2) * mm, "radius": 0.6 * mm});
            skCircle(sketch, "E10.5.0.0", {"center": v(81.54, 2.2) * mm, "radius": 0.6 * mm});
            skCircle(sketch, "E10.6.0.0", {"center": v(95.13, 2.2) * mm, "radius": 0.6 * mm});
            skCircle(sketch, "E10.7.0.0", {"center": v(108.72, 2.2) * mm, "radius": 0.6 * mm});
            skCircle(sketch, "E10.8.0.0", {"center": v(122.31, 2.2) * mm, "radius": 0.6 * mm});
            skLineSegment(sketch, "E10.direction1", {"start": v(27.18, 2.2) * mm, "end": v(40.77, 2.2) * mm, "construction": true});
            skSolve(sketch);
        }
        {
            var Q0;
            Q0=makeQuery(id+"F6.imprint","IMPRINT",FACE,{"disambiguationData":[TD([[makeQuery(id+"F6.imprint","IMPRINT",EDGE,{"derivedFrom":sQuery(id+"F6.wireOp",EDGE,"E9")}),1.0]])]});
            var Q1;
            Q1=makeQuery(id+"F6.imprint","IMPRINT",FACE,{"disambiguationData":[TD([[makeQuery(id+"F6.imprint","IMPRINT",EDGE,{"derivedFrom":sQuery(id+"F6.wireOp",EDGE,"E10.1.0.0")}),1.0]])]});
            var Q2;
            Q2=makeQuery(id+"F6.imprint","IMPRINT",FACE,{"disambiguationData":[TD([[makeQuery(id+"F6.imprint","IMPRINT",EDGE,{"derivedFrom":sQuery(id+"F6.wireOp",EDGE,"E10.2.0.0")}),1.0]])]});
            var Q3;
            Q3=makeQuery(id+"F6.imprint","IMPRINT",FACE,{"disambiguationData":[TD([[makeQuery(id+"F6.imprint","IMPRINT",EDGE,{"derivedFrom":sQuery(id+"F6.wireOp",EDGE,"E10.3.0.0")}),1.0]])]});
            var Q4;
            Q4=makeQuery(id+"F6.imprint","IMPRINT",FACE,{"disambiguationData":[TD([[makeQuery(id+"F6.imprint","IMPRINT",EDGE,{"derivedFrom":sQuery(id+"F6.wireOp",EDGE,"E10.4.0.0")}),1.0]])]});
            var Q5;
            Q5=makeQuery(id+"F6.imprint","IMPRINT",FACE,{"disambiguationData":[TD([[makeQuery(id+"F6.imprint","IMPRINT",EDGE,{"derivedFrom":sQuery(id+"F6.wireOp",EDGE,"E10.5.0.0")}),1.0]])]});
            var Q6;
            Q6=makeQuery(id+"F6.imprint","IMPRINT",FACE,{"disambiguationData":[TD([[makeQuery(id+"F6.imprint","IMPRINT",EDGE,{"derivedFrom":sQuery(id+"F6.wireOp",EDGE,"E10.6.0.0")}),1.0]])]});
            var Q7;
            Q7=makeQuery(id+"F6.imprint","IMPRINT",FACE,{"disambiguationData":[TD([[makeQuery(id+"F6.imprint","IMPRINT",EDGE,{"derivedFrom":sQuery(id+"F6.wireOp",EDGE,"E10.7.0.0")}),1.0]])]});
            var Q8;
            Q8=makeQuery(id+"F6.imprint","IMPRINT",FACE,{"disambiguationData":[TD([[makeQuery(id+"F6.imprint","IMPRINT",EDGE,{"derivedFrom":sQuery(id+"F6.wireOp",EDGE,"E10.8.0.0")}),1.0]])]});
            var Q9;
            Q9=sQuery(id+"F6.wireOp",EDGE,"E9");
            var Q10;
            Q10=sQuery(id+"F6.wireOp",EDGE,"E10.1.0.0");
            var Q11;
            Q11=sQuery(id+"F6.wireOp",EDGE,"E10.2.0.0");
            var Q12;
            Q12=sQuery(id+"F6.wireOp",EDGE,"E10.3.0.0");
            var Q13;
            Q13=sQuery(id+"F6.wireOp",EDGE,"E10.4.0.0");
            var Q14;
            Q14=sQuery(id+"F6.wireOp",EDGE,"E10.5.0.0");
            extrude(context, id + "F7", {"entities" : qUnion([Q0, Q1, Q2, Q3, Q4, Q5, Q6, Q7, Q8]), "operationType" : NewBodyOperationType.REMOVE, "surfaceEntities" : qUnion([Q9, Q10, Q11, Q12, Q13, Q14]), "oppositeDirection" : true, "depth" : 12 * mm, "offsetDistance" : 25 * mm});
        }
        {
            var Q0;
            Q0=makeQuery(id+"F5.opExtrude","CAP_EDGE",EDGE,{"disambiguationData":[OSD([sQuery(id+"F4.wireOp",EDGE,"E1.right")])],"isStart":false});
            var Q1;
            Q1=makeQuery(id+"F5.opExtrude","CAP_EDGE",EDGE,{"disambiguationData":[OSD([sQuery(id+"F4.wireOp",EDGE,"E1.left")])],"isStart":false});
            var Q2;
            Q2=makeQuery(id+"F5.opExtrude","CAP_EDGE",EDGE,{"disambiguationData":[OSD([sQuery(id+"F4.wireOp",EDGE,"E6.1.0.2")])],"isStart":false});
            var Q3;
            Q3=makeQuery(id+"F5.opExtrude","CAP_EDGE",EDGE,{"disambiguationData":[OSD([sQuery(id+"F4.wireOp",EDGE,"E6.1.0.6")])],"isStart":false});
            var Q4;
            Q4=makeQuery(id+"F5.opExtrude","CAP_EDGE",EDGE,{"disambiguationData":[OSD([sQuery(id+"F4.wireOp",EDGE,"E6.2.0.2")])],"isStart":false});
            var Q5;
            Q5=makeQuery(id+"F5.opExtrude","CAP_EDGE",EDGE,{"disambiguationData":[OSD([sQuery(id+"F4.wireOp",EDGE,"E6.2.0.6")])],"isStart":false});
            var Q6;
            Q6=makeQuery(id+"F5.opExtrude","CAP_EDGE",EDGE,{"disambiguationData":[OSD([sQuery(id+"F4.wireOp",EDGE,"E6.3.0.2")])],"isStart":false});
            var Q7;
            Q7=makeQuery(id+"F5.opExtrude","CAP_EDGE",EDGE,{"disambiguationData":[OSD([sQuery(id+"F4.wireOp",EDGE,"E6.3.0.6")])],"isStart":false});
            var Q8;
            Q8=makeQuery(id+"F5.opExtrude","CAP_EDGE",EDGE,{"disambiguationData":[OSD([sQuery(id+"F4.wireOp",EDGE,"E6.4.0.2")])],"isStart":false});
            var Q9;
            Q9=makeQuery(id+"F5.opExtrude","CAP_EDGE",EDGE,{"disambiguationData":[OSD([sQuery(id+"F4.wireOp",EDGE,"E6.4.0.6")])],"isStart":false});
            var Q10;
            Q10=makeQuery(id+"F5.opExtrude","CAP_EDGE",EDGE,{"disambiguationData":[OSD([sQuery(id+"F4.wireOp",EDGE,"E1.top")])],"isStart":false});
            var Q11;
            Q11=makeQuery(id+"F5.opExtrude","CAP_EDGE",EDGE,{"disambiguationData":[OSD([sQuery(id+"F4.wireOp",EDGE,"E1.bottom")])],"isStart":false});
            var Q12;
            Q12=makeQuery(id+"F5.opExtrude","CAP_EDGE",EDGE,{"disambiguationData":[OSD([sQuery(id+"F4.wireOp",EDGE,"E6.1.0.0")])],"isStart":false});
            var Q13;
            Q13=makeQuery(id+"F5.opExtrude","CAP_EDGE",EDGE,{"disambiguationData":[OSD([sQuery(id+"F4.wireOp",EDGE,"E6.1.0.4")])],"isStart":false});
            var Q14;
            Q14=makeQuery(id+"F5.opExtrude","CAP_EDGE",EDGE,{"disambiguationData":[OSD([sQuery(id+"F4.wireOp",EDGE,"E6.2.0.0")])],"isStart":false});
            var Q15;
            Q15=makeQuery(id+"F5.opExtrude","CAP_EDGE",EDGE,{"disambiguationData":[OSD([sQuery(id+"F4.wireOp",EDGE,"E6.2.0.4")])],"isStart":false});
            var Q16;
            Q16=makeQuery(id+"F5.opExtrude","CAP_EDGE",EDGE,{"disambiguationData":[OSD([sQuery(id+"F4.wireOp",EDGE,"E6.3.0.4")])],"isStart":false});
            var Q17;
            Q17=makeQuery(id+"F5.opExtrude","CAP_EDGE",EDGE,{"disambiguationData":[OSD([sQuery(id+"F4.wireOp",EDGE,"E6.3.0.0")])],"isStart":false});
            var Q18;
            Q18=makeQuery(id+"F5.opExtrude","CAP_EDGE",EDGE,{"disambiguationData":[OSD([sQuery(id+"F4.wireOp",EDGE,"E6.4.0.0")])],"isStart":false});
            var Q19;
            Q19=makeQuery(id+"F5.opExtrude","CAP_EDGE",EDGE,{"disambiguationData":[OSD([sQuery(id+"F4.wireOp",EDGE,"E6.4.0.4")])],"isStart":false});
            var Q20;
            Q20=makeQuery(id+"F5.opExtrude","CAP_EDGE",EDGE,{"disambiguationData":[OSD([sQuery(id+"F4.wireOp",EDGE,"E6.4.1.2")])],"isStart":false});
            var Q21;
            Q21=makeQuery(id+"F5.opExtrude","CAP_EDGE",EDGE,{"disambiguationData":[OSD([sQuery(id+"F4.wireOp",EDGE,"E6.4.1.6")])],"isStart":false});
            var Q22;
            Q22=makeQuery(id+"F5.opExtrude","CAP_EDGE",EDGE,{"disambiguationData":[OSD([sQuery(id+"F4.wireOp",EDGE,"E6.4.1.4")])],"isStart":false});
            var Q23;
            Q23=makeQuery(id+"F5.opExtrude","CAP_EDGE",EDGE,{"disambiguationData":[OSD([sQuery(id+"F4.wireOp",EDGE,"E6.4.1.0")])],"isStart":false});
            var Q24;
            Q24=makeQuery(id+"F5.opExtrude","CAP_EDGE",EDGE,{"disambiguationData":[OSD([sQuery(id+"F4.wireOp",EDGE,"E6.3.1.0")])],"isStart":false});
            var Q25;
            Q25=makeQuery(id+"F5.opExtrude","CAP_EDGE",EDGE,{"disambiguationData":[OSD([sQuery(id+"F4.wireOp",EDGE,"E6.3.1.4")])],"isStart":false});
            var Q26;
            Q26=makeQuery(id+"F5.opExtrude","CAP_EDGE",EDGE,{"disambiguationData":[OSD([sQuery(id+"F4.wireOp",EDGE,"E6.3.1.6")])],"isStart":false});
            var Q27;
            Q27=makeQuery(id+"F5.opExtrude","CAP_EDGE",EDGE,{"disambiguationData":[OSD([sQuery(id+"F4.wireOp",EDGE,"E6.3.1.2")])],"isStart":false});
            var Q28;
            Q28=makeQuery(id+"F5.opExtrude","CAP_EDGE",EDGE,{"disambiguationData":[OSD([sQuery(id+"F4.wireOp",EDGE,"E6.2.1.6")])],"isStart":false});
            var Q29;
            Q29=makeQuery(id+"F5.opExtrude","CAP_EDGE",EDGE,{"disambiguationData":[OSD([sQuery(id+"F4.wireOp",EDGE,"E6.2.1.4")])],"isStart":false});
            var Q30;
            Q30=makeQuery(id+"F5.opExtrude","CAP_EDGE",EDGE,{"disambiguationData":[OSD([sQuery(id+"F4.wireOp",EDGE,"E6.2.1.0")])],"isStart":false});
            var Q31;
            Q31=makeQuery(id+"F5.opExtrude","CAP_EDGE",EDGE,{"disambiguationData":[OSD([sQuery(id+"F4.wireOp",EDGE,"E6.2.1.2")])],"isStart":false});
            var Q32;
            Q32=makeQuery(id+"F5.opExtrude","CAP_EDGE",EDGE,{"disambiguationData":[OSD([sQuery(id+"F4.wireOp",EDGE,"E6.1.1.6")])],"isStart":false});
            var Q33;
            Q33=makeQuery(id+"F5.opExtrude","CAP_EDGE",EDGE,{"disambiguationData":[OSD([sQuery(id+"F4.wireOp",EDGE,"E6.1.1.4")])],"isStart":false});
            var Q34;
            Q34=makeQuery(id+"F5.opExtrude","CAP_EDGE",EDGE,{"disambiguationData":[OSD([sQuery(id+"F4.wireOp",EDGE,"E6.1.1.0")])],"isStart":false});
            var Q35;
            Q35=makeQuery(id+"F5.opExtrude","CAP_EDGE",EDGE,{"disambiguationData":[OSD([sQuery(id+"F4.wireOp",EDGE,"E6.1.1.2")])],"isStart":false});
            var Q36;
            Q36=makeQuery(id+"F5.opExtrude","CAP_EDGE",EDGE,{"disambiguationData":[OSD([sQuery(id+"F4.wireOp",EDGE,"E6.0.1.6")])],"isStart":false});
            var Q37;
            Q37=makeQuery(id+"F5.opExtrude","CAP_EDGE",EDGE,{"disambiguationData":[OSD([sQuery(id+"F4.wireOp",EDGE,"E6.0.1.2")])],"isStart":false});
            var Q38;
            Q38=makeQuery(id+"F5.opExtrude","CAP_EDGE",EDGE,{"disambiguationData":[OSD([sQuery(id+"F4.wireOp",EDGE,"E6.0.1.4")])],"isStart":false});
            var Q39;
            Q39=makeQuery(id+"F5.opExtrude","CAP_EDGE",EDGE,{"disambiguationData":[OSD([sQuery(id+"F4.wireOp",EDGE,"E6.0.1.0")])],"isStart":false});
            var Q40;
            Q40=makeQuery(id+"F5.opExtrude","CAP_EDGE",EDGE,{"disambiguationData":[OSD([sQuery(id+"F4.wireOp",EDGE,"E6.0.2.4")])],"isStart":false});
            var Q41;
            Q41=makeQuery(id+"F5.opExtrude","CAP_EDGE",EDGE,{"disambiguationData":[OSD([sQuery(id+"F4.wireOp",EDGE,"E6.0.2.2")])],"isStart":false});
            var Q42;
            Q42=makeQuery(id+"F5.opExtrude","CAP_EDGE",EDGE,{"disambiguationData":[OSD([sQuery(id+"F4.wireOp",EDGE,"E6.0.2.0")])],"isStart":false});
            var Q43;
            Q43=makeQuery(id+"F5.opExtrude","CAP_EDGE",EDGE,{"disambiguationData":[OSD([sQuery(id+"F4.wireOp",EDGE,"E6.0.2.6")])],"isStart":false});
            var Q44;
            Q44=makeQuery(id+"F5.opExtrude","CAP_EDGE",EDGE,{"disambiguationData":[OSD([sQuery(id+"F4.wireOp",EDGE,"E6.1.2.4")])],"isStart":false});
            var Q45;
            Q45=makeQuery(id+"F5.opExtrude","CAP_EDGE",EDGE,{"disambiguationData":[OSD([sQuery(id+"F4.wireOp",EDGE,"E6.1.2.0")])],"isStart":false});
            var Q46;
            Q46=makeQuery(id+"F5.opExtrude","CAP_EDGE",EDGE,{"disambiguationData":[OSD([sQuery(id+"F4.wireOp",EDGE,"E6.1.2.2")])],"isStart":false});
            var Q47;
            Q47=makeQuery(id+"F5.opExtrude","CAP_EDGE",EDGE,{"disambiguationData":[OSD([sQuery(id+"F4.wireOp",EDGE,"E6.1.2.6")])],"isStart":false});
            var Q48;
            Q48=makeQuery(id+"F5.opExtrude","CAP_EDGE",EDGE,{"disambiguationData":[OSD([sQuery(id+"F4.wireOp",EDGE,"E6.2.2.2")])],"isStart":false});
            var Q49;
            Q49=makeQuery(id+"F5.opExtrude","CAP_EDGE",EDGE,{"disambiguationData":[OSD([sQuery(id+"F4.wireOp",EDGE,"E6.2.2.4")])],"isStart":false});
            var Q50;
            Q50=makeQuery(id+"F5.opExtrude","CAP_EDGE",EDGE,{"disambiguationData":[OSD([sQuery(id+"F4.wireOp",EDGE,"E6.2.2.6")])],"isStart":false});
            var Q51;
            Q51=makeQuery(id+"F5.opExtrude","CAP_EDGE",EDGE,{"disambiguationData":[OSD([sQuery(id+"F4.wireOp",EDGE,"E6.2.2.0")])],"isStart":false});
            var Q52;
            Q52=makeQuery(id+"F5.opExtrude","CAP_EDGE",EDGE,{"disambiguationData":[OSD([sQuery(id+"F4.wireOp",EDGE,"E6.3.2.2")])],"isStart":false});
            var Q53;
            Q53=makeQuery(id+"F5.opExtrude","CAP_EDGE",EDGE,{"disambiguationData":[OSD([sQuery(id+"F4.wireOp",EDGE,"E6.3.2.4")])],"isStart":false});
            var Q54;
            Q54=makeQuery(id+"F5.opExtrude","CAP_EDGE",EDGE,{"disambiguationData":[OSD([sQuery(id+"F4.wireOp",EDGE,"E6.3.2.6")])],"isStart":false});
            var Q55;
            Q55=makeQuery(id+"F5.opExtrude","CAP_EDGE",EDGE,{"disambiguationData":[OSD([sQuery(id+"F4.wireOp",EDGE,"E6.3.2.0")])],"isStart":false});
            var Q56;
            Q56=makeQuery(id+"F5.opExtrude","CAP_EDGE",EDGE,{"disambiguationData":[OSD([sQuery(id+"F4.wireOp",EDGE,"E6.4.2.4")])],"isStart":false});
            var Q57;
            Q57=makeQuery(id+"F5.opExtrude","CAP_EDGE",EDGE,{"disambiguationData":[OSD([sQuery(id+"F4.wireOp",EDGE,"E6.4.2.2")])],"isStart":false});
            var Q58;
            Q58=makeQuery(id+"F5.opExtrude","CAP_EDGE",EDGE,{"disambiguationData":[OSD([sQuery(id+"F4.wireOp",EDGE,"E6.4.2.6")])],"isStart":false});
            var Q59;
            Q59=makeQuery(id+"F5.opExtrude","CAP_EDGE",EDGE,{"disambiguationData":[OSD([sQuery(id+"F4.wireOp",EDGE,"E6.4.2.0")])],"isStart":false});
            var Q60;
            Q60=makeQuery(id+"F5.opExtrude","CAP_EDGE",EDGE,{"disambiguationData":[OSD([sQuery(id+"F4.wireOp",EDGE,"E6.0.3.4")])],"isStart":false});
            var Q61;
            Q61=makeQuery(id+"F5.opExtrude","CAP_EDGE",EDGE,{"disambiguationData":[OSD([sQuery(id+"F4.wireOp",EDGE,"E6.0.3.2")])],"isStart":false});
            var Q62;
            Q62=makeQuery(id+"F5.opExtrude","CAP_EDGE",EDGE,{"disambiguationData":[OSD([sQuery(id+"F4.wireOp",EDGE,"E6.0.3.6")])],"isStart":false});
            var Q63;
            Q63=makeQuery(id+"F5.opExtrude","CAP_EDGE",EDGE,{"disambiguationData":[OSD([sQuery(id+"F4.wireOp",EDGE,"E6.1.3.2")])],"isStart":false});
            var Q64;
            Q64=makeQuery(id+"F5.opExtrude","CAP_EDGE",EDGE,{"disambiguationData":[OSD([sQuery(id+"F4.wireOp",EDGE,"E6.1.3.4")])],"isStart":false});
            var Q65;
            Q65=makeQuery(id+"F5.opExtrude","CAP_EDGE",EDGE,{"disambiguationData":[OSD([sQuery(id+"F4.wireOp",EDGE,"E6.1.3.6")])],"isStart":false});
            var Q66;
            Q66=makeQuery(id+"F5.opExtrude","CAP_EDGE",EDGE,{"disambiguationData":[OSD([sQuery(id+"F4.wireOp",EDGE,"E6.2.3.2")])],"isStart":false});
            var Q67;
            Q67=makeQuery(id+"F5.opExtrude","CAP_EDGE",EDGE,{"disambiguationData":[OSD([sQuery(id+"F4.wireOp",EDGE,"E6.2.3.4")])],"isStart":false});
            var Q68;
            Q68=makeQuery(id+"F5.opExtrude","CAP_EDGE",EDGE,{"disambiguationData":[OSD([sQuery(id+"F4.wireOp",EDGE,"E6.2.3.6")])],"isStart":false});
            var Q69;
            Q69=makeQuery(id+"F5.opExtrude","CAP_EDGE",EDGE,{"disambiguationData":[OSD([sQuery(id+"F4.wireOp",EDGE,"E6.3.3.2")])],"isStart":false});
            var Q70;
            Q70=makeQuery(id+"F5.opExtrude","CAP_EDGE",EDGE,{"disambiguationData":[OSD([sQuery(id+"F4.wireOp",EDGE,"E6.3.3.4")])],"isStart":false});
            var Q71;
            Q71=makeQuery(id+"F5.opExtrude","CAP_EDGE",EDGE,{"disambiguationData":[OSD([sQuery(id+"F4.wireOp",EDGE,"E6.3.3.6")])],"isStart":false});
            var Q72;
            Q72=makeQuery(id+"F5.opExtrude","CAP_EDGE",EDGE,{"disambiguationData":[OSD([sQuery(id+"F4.wireOp",EDGE,"E6.4.3.2")])],"isStart":false});
            var Q73;
            Q73=makeQuery(id+"F5.opExtrude","CAP_EDGE",EDGE,{"disambiguationData":[OSD([sQuery(id+"F4.wireOp",EDGE,"E6.4.3.4")])],"isStart":false});
            var Q74;
            Q74=makeQuery(id+"F5.opExtrude","CAP_EDGE",EDGE,{"disambiguationData":[OSD([sQuery(id+"F4.wireOp",EDGE,"E6.4.3.6")])],"isStart":false});
            var Q75;
            Q75=makeQuery(id+"F5.opExtrude","CAP_EDGE",EDGE,{"disambiguationData":[OSD([sQuery(id+"F4.wireOp",EDGE,"E6.0.3.0")])],"isStart":false});
            var Q76;
            Q76=makeQuery(id+"F5.opExtrude","CAP_EDGE",EDGE,{"disambiguationData":[OSD([sQuery(id+"F4.wireOp",EDGE,"E6.1.3.0")])],"isStart":false});
            var Q77;
            Q77=makeQuery(id+"F5.opExtrude","CAP_EDGE",EDGE,{"disambiguationData":[OSD([sQuery(id+"F4.wireOp",EDGE,"E6.2.3.0")])],"isStart":false});
            var Q78;
            Q78=makeQuery(id+"F5.opExtrude","CAP_EDGE",EDGE,{"disambiguationData":[OSD([sQuery(id+"F4.wireOp",EDGE,"E6.3.3.0")])],"isStart":false});
            var Q79;
            Q79=makeQuery(id+"F5.opExtrude","CAP_EDGE",EDGE,{"disambiguationData":[OSD([sQuery(id+"F4.wireOp",EDGE,"E6.4.3.0")])],"isStart":false});
            var Q80;
            Q80=makeQuery(id+"F5.opExtrude","CAP_EDGE",EDGE,{"disambiguationData":[OSD([sQuery(id+"F4.wireOp",EDGE,"E6.4.4.4")])],"isStart":false});
            var Q81;
            Q81=makeQuery(id+"F5.opExtrude","CAP_EDGE",EDGE,{"disambiguationData":[OSD([sQuery(id+"F4.wireOp",EDGE,"E6.4.4.6")])],"isStart":false});
            var Q82;
            Q82=makeQuery(id+"F5.opExtrude","CAP_EDGE",EDGE,{"disambiguationData":[OSD([sQuery(id+"F4.wireOp",EDGE,"E6.4.4.0")])],"isStart":false});
            var Q83;
            Q83=makeQuery(id+"F5.opExtrude","CAP_EDGE",EDGE,{"disambiguationData":[OSD([sQuery(id+"F4.wireOp",EDGE,"E6.4.4.2")])],"isStart":false});
            var Q84;
            Q84=makeQuery(id+"F5.opExtrude","CAP_EDGE",EDGE,{"disambiguationData":[OSD([sQuery(id+"F4.wireOp",EDGE,"E6.3.4.6")])],"isStart":false});
            var Q85;
            Q85=makeQuery(id+"F5.opExtrude","CAP_EDGE",EDGE,{"disambiguationData":[OSD([sQuery(id+"F4.wireOp",EDGE,"E6.3.4.4")])],"isStart":false});
            var Q86;
            Q86=makeQuery(id+"F5.opExtrude","CAP_EDGE",EDGE,{"disambiguationData":[OSD([sQuery(id+"F4.wireOp",EDGE,"E6.3.4.2")])],"isStart":false});
            var Q87;
            Q87=makeQuery(id+"F5.opExtrude","CAP_EDGE",EDGE,{"disambiguationData":[OSD([sQuery(id+"F4.wireOp",EDGE,"E6.3.4.0")])],"isStart":false});
            var Q88;
            Q88=makeQuery(id+"F5.opExtrude","CAP_EDGE",EDGE,{"disambiguationData":[OSD([sQuery(id+"F4.wireOp",EDGE,"E6.2.4.6")])],"isStart":false});
            var Q89;
            Q89=makeQuery(id+"F5.opExtrude","CAP_EDGE",EDGE,{"disambiguationData":[OSD([sQuery(id+"F4.wireOp",EDGE,"E6.2.4.4")])],"isStart":false});
            var Q90;
            Q90=makeQuery(id+"F5.opExtrude","CAP_EDGE",EDGE,{"disambiguationData":[OSD([sQuery(id+"F4.wireOp",EDGE,"E6.2.4.0")])],"isStart":false});
            var Q91;
            Q91=makeQuery(id+"F5.opExtrude","CAP_EDGE",EDGE,{"disambiguationData":[OSD([sQuery(id+"F4.wireOp",EDGE,"E6.2.4.2")])],"isStart":false});
            var Q92;
            Q92=makeQuery(id+"F5.opExtrude","CAP_EDGE",EDGE,{"disambiguationData":[OSD([sQuery(id+"F4.wireOp",EDGE,"E6.1.4.6")])],"isStart":false});
            var Q93;
            Q93=makeQuery(id+"F5.opExtrude","CAP_EDGE",EDGE,{"disambiguationData":[OSD([sQuery(id+"F4.wireOp",EDGE,"E6.1.4.4")])],"isStart":false});
            var Q94;
            Q94=makeQuery(id+"F5.opExtrude","CAP_EDGE",EDGE,{"disambiguationData":[OSD([sQuery(id+"F4.wireOp",EDGE,"E6.1.4.2")])],"isStart":false});
            var Q95;
            Q95=makeQuery(id+"F5.opExtrude","CAP_EDGE",EDGE,{"disambiguationData":[OSD([sQuery(id+"F4.wireOp",EDGE,"E6.1.4.0")])],"isStart":false});
            var Q96;
            Q96=makeQuery(id+"F5.opExtrude","CAP_EDGE",EDGE,{"disambiguationData":[OSD([sQuery(id+"F4.wireOp",EDGE,"E6.0.4.6")])],"isStart":false});
            var Q97;
            Q97=makeQuery(id+"F5.opExtrude","CAP_EDGE",EDGE,{"disambiguationData":[OSD([sQuery(id+"F4.wireOp",EDGE,"E6.0.4.4")])],"isStart":false});
            var Q98;
            Q98=makeQuery(id+"F5.opExtrude","CAP_EDGE",EDGE,{"disambiguationData":[OSD([sQuery(id+"F4.wireOp",EDGE,"E6.0.4.2")])],"isStart":false});
            var Q99;
            Q99=makeQuery(id+"F5.opExtrude","CAP_EDGE",EDGE,{"disambiguationData":[OSD([sQuery(id+"F4.wireOp",EDGE,"E6.0.4.0")])],"isStart":false});
            var Q100;
            Q100=makeQuery(id+"F5.opExtrude","CAP_EDGE",EDGE,{"disambiguationData":[OSD([sQuery(id+"F4.wireOp",EDGE,"E2")])],"isStart":false});
            var Q101;
            Q101=makeQuery(id+"F5.opExtrude","CAP_EDGE",EDGE,{"disambiguationData":[OSD([sQuery(id+"F4.wireOp",EDGE,"E3")])],"isStart":false});
            var Q102;
            Q102=makeQuery(id+"F5.opExtrude","CAP_EDGE",EDGE,{"disambiguationData":[OSD([sQuery(id+"F4.wireOp",EDGE,"E5")])],"isStart":false});
            var Q103;
            Q103=makeQuery(id+"F5.opExtrude","CAP_EDGE",EDGE,{"disambiguationData":[OSD([sQuery(id+"F4.wireOp",EDGE,"E4")])],"isStart":false});
            var Q104;
            Q104=makeQuery(id+"F5.opExtrude","CAP_EDGE",EDGE,{"disambiguationData":[OSD([sQuery(id+"F4.wireOp",EDGE,"E6.1.0.3")])],"isStart":false});
            var Q105;
            Q105=makeQuery(id+"F5.opExtrude","CAP_EDGE",EDGE,{"disambiguationData":[OSD([sQuery(id+"F4.wireOp",EDGE,"E6.1.0.5")])],"isStart":false});
            var Q106;
            Q106=makeQuery(id+"F5.opExtrude","CAP_EDGE",EDGE,{"disambiguationData":[OSD([sQuery(id+"F4.wireOp",EDGE,"E6.1.0.7")])],"isStart":false});
            var Q107;
            Q107=makeQuery(id+"F5.opExtrude","CAP_EDGE",EDGE,{"disambiguationData":[OSD([sQuery(id+"F4.wireOp",EDGE,"E6.1.0.1")])],"isStart":false});
            var Q108;
            Q108=makeQuery(id+"F5.opExtrude","CAP_EDGE",EDGE,{"disambiguationData":[OSD([sQuery(id+"F4.wireOp",EDGE,"E6.2.0.1")])],"isStart":false});
            var Q109;
            Q109=makeQuery(id+"F5.opExtrude","CAP_EDGE",EDGE,{"disambiguationData":[OSD([sQuery(id+"F4.wireOp",EDGE,"E6.2.0.3")])],"isStart":false});
            var Q110;
            Q110=makeQuery(id+"F5.opExtrude","CAP_EDGE",EDGE,{"disambiguationData":[OSD([sQuery(id+"F4.wireOp",EDGE,"E6.2.0.5")])],"isStart":false});
            var Q111;
            Q111=makeQuery(id+"F5.opExtrude","CAP_EDGE",EDGE,{"disambiguationData":[OSD([sQuery(id+"F4.wireOp",EDGE,"E6.2.0.7")])],"isStart":false});
            var Q112;
            Q112=makeQuery(id+"F5.opExtrude","CAP_EDGE",EDGE,{"disambiguationData":[OSD([sQuery(id+"F4.wireOp",EDGE,"E6.3.0.3")])],"isStart":false});
            var Q113;
            Q113=makeQuery(id+"F5.opExtrude","CAP_EDGE",EDGE,{"disambiguationData":[OSD([sQuery(id+"F4.wireOp",EDGE,"E6.3.0.5")])],"isStart":false});
            var Q114;
            Q114=makeQuery(id+"F5.opExtrude","CAP_EDGE",EDGE,{"disambiguationData":[OSD([sQuery(id+"F4.wireOp",EDGE,"E6.3.0.7")])],"isStart":false});
            var Q115;
            Q115=makeQuery(id+"F5.opExtrude","CAP_EDGE",EDGE,{"disambiguationData":[OSD([sQuery(id+"F4.wireOp",EDGE,"E6.3.0.1")])],"isStart":false});
            var Q116;
            Q116=makeQuery(id+"F5.opExtrude","CAP_EDGE",EDGE,{"disambiguationData":[OSD([sQuery(id+"F4.wireOp",EDGE,"E6.4.0.3")])],"isStart":false});
            var Q117;
            Q117=makeQuery(id+"F5.opExtrude","CAP_EDGE",EDGE,{"disambiguationData":[OSD([sQuery(id+"F4.wireOp",EDGE,"E6.4.0.1")])],"isStart":false});
            var Q118;
            Q118=makeQuery(id+"F5.opExtrude","CAP_EDGE",EDGE,{"disambiguationData":[OSD([sQuery(id+"F4.wireOp",EDGE,"E6.4.0.5")])],"isStart":false});
            var Q119;
            Q119=makeQuery(id+"F5.opExtrude","CAP_EDGE",EDGE,{"disambiguationData":[OSD([sQuery(id+"F4.wireOp",EDGE,"E6.4.0.7")])],"isStart":false});
            var Q120;
            Q120=makeQuery(id+"F5.opExtrude","CAP_EDGE",EDGE,{"disambiguationData":[OSD([sQuery(id+"F4.wireOp",EDGE,"E7.5.5.0")])],"isStart":false});
            var Q121;
            Q121=makeQuery(id+"F5.opExtrude","CAP_EDGE",EDGE,{"disambiguationData":[OSD([sQuery(id+"F4.wireOp",EDGE,"E7.8.5.0")])],"isStart":false});
            var Q122;
            Q122=makeQuery(id+"F5.opExtrude","CAP_EDGE",EDGE,{"disambiguationData":[OSD([sQuery(id+"F4.wireOp",EDGE,"E7.10.5.0")])],"isStart":false});
            var Q123;
            Q123=makeQuery(id+"F5.opExtrude","CAP_EDGE",EDGE,{"disambiguationData":[OSD([sQuery(id+"F4.wireOp",EDGE,"E7.13.5.0")])],"isStart":false});
            var Q124;
            Q124=makeQuery(id+"F5.opExtrude","CAP_EDGE",EDGE,{"disambiguationData":[OSD([sQuery(id+"F4.wireOp",EDGE,"E7.15.5.0")])],"isStart":false});
            var Q125;
            Q125=makeQuery(id+"F5.opExtrude","CAP_EDGE",EDGE,{"disambiguationData":[OSD([sQuery(id+"F4.wireOp",EDGE,"E7.18.5.0")])],"isStart":false});
            var Q126;
            Q126=makeQuery(id+"F5.opExtrude","CAP_EDGE",EDGE,{"disambiguationData":[OSD([sQuery(id+"F4.wireOp",EDGE,"E7.0.5.0")])],"isStart":false});
            var Q127;
            Q127=makeQuery(id+"F5.opExtrude","CAP_EDGE",EDGE,{"disambiguationData":[OSD([sQuery(id+"F4.wireOp",EDGE,"E7.3.5.0")])],"isStart":false});
            var Q128;
            Q128=makeQuery(id+"F5.opExtrude","CAP_EDGE",EDGE,{"disambiguationData":[OSD([sQuery(id+"F4.wireOp",EDGE,"E7.5.6.0")])],"isStart":false});
            var Q129;
            Q129=makeQuery(id+"F5.opExtrude","CAP_EDGE",EDGE,{"disambiguationData":[OSD([sQuery(id+"F4.wireOp",EDGE,"E7.8.6.0")])],"isStart":false});
            var Q130;
            Q130=makeQuery(id+"F5.opExtrude","CAP_EDGE",EDGE,{"disambiguationData":[OSD([sQuery(id+"F4.wireOp",EDGE,"E7.10.6.0")])],"isStart":false});
            var Q131;
            Q131=makeQuery(id+"F5.opExtrude","CAP_EDGE",EDGE,{"disambiguationData":[OSD([sQuery(id+"F4.wireOp",EDGE,"E7.13.6.0")])],"isStart":false});
            var Q132;
            Q132=makeQuery(id+"F5.opExtrude","CAP_EDGE",EDGE,{"disambiguationData":[OSD([sQuery(id+"F4.wireOp",EDGE,"E7.15.6.0")])],"isStart":false});
            var Q133;
            Q133=makeQuery(id+"F5.opExtrude","CAP_EDGE",EDGE,{"disambiguationData":[OSD([sQuery(id+"F4.wireOp",EDGE,"E7.18.6.0")])],"isStart":false});
            var Q134;
            Q134=makeQuery(id+"F5.opExtrude","CAP_EDGE",EDGE,{"disambiguationData":[OSD([sQuery(id+"F4.wireOp",EDGE,"E7.0.6.0")])],"isStart":false});
            var Q135;
            Q135=makeQuery(id+"F5.opExtrude","CAP_EDGE",EDGE,{"disambiguationData":[OSD([sQuery(id+"F4.wireOp",EDGE,"E7.3.6.0")])],"isStart":false});
            var Q136;
            Q136=makeQuery(id+"F5.opExtrude","CAP_EDGE",EDGE,{"disambiguationData":[OSD([sQuery(id+"F4.wireOp",EDGE,"E6.0.1.1")])],"isStart":false});
            var Q137;
            Q137=makeQuery(id+"F5.opExtrude","CAP_EDGE",EDGE,{"disambiguationData":[OSD([sQuery(id+"F4.wireOp",EDGE,"E6.0.1.3")])],"isStart":false});
            var Q138;
            Q138=makeQuery(id+"F5.opExtrude","CAP_EDGE",EDGE,{"disambiguationData":[OSD([sQuery(id+"F4.wireOp",EDGE,"E6.0.1.5")])],"isStart":false});
            var Q139;
            Q139=makeQuery(id+"F5.opExtrude","CAP_EDGE",EDGE,{"disambiguationData":[OSD([sQuery(id+"F4.wireOp",EDGE,"E6.0.1.7")])],"isStart":false});
            var Q140;
            Q140=makeQuery(id+"F5.opExtrude","CAP_EDGE",EDGE,{"disambiguationData":[OSD([sQuery(id+"F4.wireOp",EDGE,"E6.1.1.1")])],"isStart":false});
            var Q141;
            Q141=makeQuery(id+"F5.opExtrude","CAP_EDGE",EDGE,{"disambiguationData":[OSD([sQuery(id+"F4.wireOp",EDGE,"E6.1.1.3")])],"isStart":false});
            var Q142;
            Q142=makeQuery(id+"F5.opExtrude","CAP_EDGE",EDGE,{"disambiguationData":[OSD([sQuery(id+"F4.wireOp",EDGE,"E6.1.1.5")])],"isStart":false});
            var Q143;
            Q143=makeQuery(id+"F5.opExtrude","CAP_EDGE",EDGE,{"disambiguationData":[OSD([sQuery(id+"F4.wireOp",EDGE,"E6.1.1.7")])],"isStart":false});
            var Q144;
            Q144=makeQuery(id+"F5.opExtrude","CAP_EDGE",EDGE,{"disambiguationData":[OSD([sQuery(id+"F4.wireOp",EDGE,"E6.2.1.1")])],"isStart":false});
            var Q145;
            Q145=makeQuery(id+"F5.opExtrude","CAP_EDGE",EDGE,{"disambiguationData":[OSD([sQuery(id+"F4.wireOp",EDGE,"E6.2.1.3")])],"isStart":false});
            var Q146;
            Q146=makeQuery(id+"F5.opExtrude","CAP_EDGE",EDGE,{"disambiguationData":[OSD([sQuery(id+"F4.wireOp",EDGE,"E6.2.1.5")])],"isStart":false});
            var Q147;
            Q147=makeQuery(id+"F5.opExtrude","CAP_EDGE",EDGE,{"disambiguationData":[OSD([sQuery(id+"F4.wireOp",EDGE,"E6.2.1.7")])],"isStart":false});
            var Q148;
            Q148=makeQuery(id+"F5.opExtrude","CAP_EDGE",EDGE,{"disambiguationData":[OSD([sQuery(id+"F4.wireOp",EDGE,"E6.3.1.1")])],"isStart":false});
            var Q149;
            Q149=makeQuery(id+"F5.opExtrude","CAP_EDGE",EDGE,{"disambiguationData":[OSD([sQuery(id+"F4.wireOp",EDGE,"E6.3.1.3")])],"isStart":false});
            var Q150;
            Q150=makeQuery(id+"F5.opExtrude","CAP_EDGE",EDGE,{"disambiguationData":[OSD([sQuery(id+"F4.wireOp",EDGE,"E6.3.1.5")])],"isStart":false});
            var Q151;
            Q151=makeQuery(id+"F5.opExtrude","CAP_EDGE",EDGE,{"disambiguationData":[OSD([sQuery(id+"F4.wireOp",EDGE,"E6.3.1.7")])],"isStart":false});
            var Q152;
            Q152=makeQuery(id+"F5.opExtrude","CAP_EDGE",EDGE,{"disambiguationData":[OSD([sQuery(id+"F4.wireOp",EDGE,"E6.4.1.1")])],"isStart":false});
            var Q153;
            Q153=makeQuery(id+"F5.opExtrude","CAP_EDGE",EDGE,{"disambiguationData":[OSD([sQuery(id+"F4.wireOp",EDGE,"E6.4.1.3")])],"isStart":false});
            var Q154;
            Q154=makeQuery(id+"F5.opExtrude","CAP_EDGE",EDGE,{"disambiguationData":[OSD([sQuery(id+"F4.wireOp",EDGE,"E6.4.1.5")])],"isStart":false});
            var Q155;
            Q155=makeQuery(id+"F5.opExtrude","CAP_EDGE",EDGE,{"disambiguationData":[OSD([sQuery(id+"F4.wireOp",EDGE,"E6.4.1.7")])],"isStart":false});
            var Q156;
            Q156=makeQuery(id+"F5.opExtrude","CAP_EDGE",EDGE,{"disambiguationData":[OSD([sQuery(id+"F4.wireOp",EDGE,"E7.3.5.1")])],"isStart":false});
            var Q157;
            Q157=makeQuery(id+"F5.opExtrude","CAP_EDGE",EDGE,{"disambiguationData":[OSD([sQuery(id+"F4.wireOp",EDGE,"E7.5.5.1")])],"isStart":false});
            var Q158;
            Q158=makeQuery(id+"F5.opExtrude","CAP_EDGE",EDGE,{"disambiguationData":[OSD([sQuery(id+"F4.wireOp",EDGE,"E7.8.5.1")])],"isStart":false});
            var Q159;
            Q159=makeQuery(id+"F5.opExtrude","CAP_EDGE",EDGE,{"disambiguationData":[OSD([sQuery(id+"F4.wireOp",EDGE,"E7.13.5.1")])],"isStart":false});
            var Q160;
            Q160=makeQuery(id+"F5.opExtrude","CAP_EDGE",EDGE,{"disambiguationData":[OSD([sQuery(id+"F4.wireOp",EDGE,"E7.10.5.1")])],"isStart":false});
            var Q161;
            Q161=makeQuery(id+"F5.opExtrude","CAP_EDGE",EDGE,{"disambiguationData":[OSD([sQuery(id+"F4.wireOp",EDGE,"E7.15.5.1")])],"isStart":false});
            var Q162;
            Q162=makeQuery(id+"F5.opExtrude","CAP_EDGE",EDGE,{"disambiguationData":[OSD([sQuery(id+"F4.wireOp",EDGE,"E7.18.5.1")])],"isStart":false});
            var Q163;
            Q163=makeQuery(id+"F5.opExtrude","CAP_EDGE",EDGE,{"disambiguationData":[OSD([sQuery(id+"F4.wireOp",EDGE,"E7.0.5.1")])],"isStart":false});
            var Q164;
            Q164=makeQuery(id+"F5.opExtrude","CAP_EDGE",EDGE,{"disambiguationData":[OSD([sQuery(id+"F4.wireOp",EDGE,"E7.5.6.1")])],"isStart":false});
            var Q165;
            Q165=makeQuery(id+"F5.opExtrude","CAP_EDGE",EDGE,{"disambiguationData":[OSD([sQuery(id+"F4.wireOp",EDGE,"E7.8.6.1")])],"isStart":false});
            var Q166;
            Q166=makeQuery(id+"F5.opExtrude","CAP_EDGE",EDGE,{"disambiguationData":[OSD([sQuery(id+"F4.wireOp",EDGE,"E7.10.6.1")])],"isStart":false});
            var Q167;
            Q167=makeQuery(id+"F5.opExtrude","CAP_EDGE",EDGE,{"disambiguationData":[OSD([sQuery(id+"F4.wireOp",EDGE,"E7.13.6.1")])],"isStart":false});
            var Q168;
            Q168=makeQuery(id+"F5.opExtrude","CAP_EDGE",EDGE,{"disambiguationData":[OSD([sQuery(id+"F4.wireOp",EDGE,"E7.15.6.1")])],"isStart":false});
            var Q169;
            Q169=makeQuery(id+"F5.opExtrude","CAP_EDGE",EDGE,{"disambiguationData":[OSD([sQuery(id+"F4.wireOp",EDGE,"E7.18.6.1")])],"isStart":false});
            var Q170;
            Q170=makeQuery(id+"F5.opExtrude","CAP_EDGE",EDGE,{"disambiguationData":[OSD([sQuery(id+"F4.wireOp",EDGE,"E7.0.6.1")])],"isStart":false});
            var Q171;
            Q171=makeQuery(id+"F5.opExtrude","CAP_EDGE",EDGE,{"disambiguationData":[OSD([sQuery(id+"F4.wireOp",EDGE,"E7.3.6.1")])],"isStart":false});
            var Q172;
            Q172=makeQuery(id+"F5.opExtrude","CAP_EDGE",EDGE,{"disambiguationData":[OSD([sQuery(id+"F4.wireOp",EDGE,"E6.0.2.1")])],"isStart":false});
            var Q173;
            Q173=makeQuery(id+"F5.opExtrude","CAP_EDGE",EDGE,{"disambiguationData":[OSD([sQuery(id+"F4.wireOp",EDGE,"E6.0.2.3")])],"isStart":false});
            var Q174;
            Q174=makeQuery(id+"F5.opExtrude","CAP_EDGE",EDGE,{"disambiguationData":[OSD([sQuery(id+"F4.wireOp",EDGE,"E6.0.2.5")])],"isStart":false});
            var Q175;
            Q175=makeQuery(id+"F5.opExtrude","CAP_EDGE",EDGE,{"disambiguationData":[OSD([sQuery(id+"F4.wireOp",EDGE,"E6.0.2.7")])],"isStart":false});
            var Q176;
            Q176=makeQuery(id+"F5.opExtrude","CAP_EDGE",EDGE,{"disambiguationData":[OSD([sQuery(id+"F4.wireOp",EDGE,"E6.1.2.1")])],"isStart":false});
            var Q177;
            Q177=makeQuery(id+"F5.opExtrude","CAP_EDGE",EDGE,{"disambiguationData":[OSD([sQuery(id+"F4.wireOp",EDGE,"E6.1.2.3")])],"isStart":false});
            var Q178;
            Q178=makeQuery(id+"F5.opExtrude","CAP_EDGE",EDGE,{"disambiguationData":[OSD([sQuery(id+"F4.wireOp",EDGE,"E6.1.2.5")])],"isStart":false});
            var Q179;
            Q179=makeQuery(id+"F5.opExtrude","CAP_EDGE",EDGE,{"disambiguationData":[OSD([sQuery(id+"F4.wireOp",EDGE,"E6.1.2.7")])],"isStart":false});
            var Q180;
            Q180=makeQuery(id+"F5.opExtrude","CAP_EDGE",EDGE,{"disambiguationData":[OSD([sQuery(id+"F4.wireOp",EDGE,"E6.2.2.1")])],"isStart":false});
            var Q181;
            Q181=makeQuery(id+"F5.opExtrude","CAP_EDGE",EDGE,{"disambiguationData":[OSD([sQuery(id+"F4.wireOp",EDGE,"E6.2.2.3")])],"isStart":false});
            var Q182;
            Q182=makeQuery(id+"F5.opExtrude","CAP_EDGE",EDGE,{"disambiguationData":[OSD([sQuery(id+"F4.wireOp",EDGE,"E6.2.2.5")])],"isStart":false});
            var Q183;
            Q183=makeQuery(id+"F5.opExtrude","CAP_EDGE",EDGE,{"disambiguationData":[OSD([sQuery(id+"F4.wireOp",EDGE,"E6.2.2.7")])],"isStart":false});
            var Q184;
            Q184=makeQuery(id+"F5.opExtrude","CAP_EDGE",EDGE,{"disambiguationData":[OSD([sQuery(id+"F4.wireOp",EDGE,"E6.3.2.1")])],"isStart":false});
            var Q185;
            Q185=makeQuery(id+"F5.opExtrude","CAP_EDGE",EDGE,{"disambiguationData":[OSD([sQuery(id+"F4.wireOp",EDGE,"E6.3.2.3")])],"isStart":false});
            var Q186;
            Q186=makeQuery(id+"F5.opExtrude","CAP_EDGE",EDGE,{"disambiguationData":[OSD([sQuery(id+"F4.wireOp",EDGE,"E6.3.2.5")])],"isStart":false});
            var Q187;
            Q187=makeQuery(id+"F5.opExtrude","CAP_EDGE",EDGE,{"disambiguationData":[OSD([sQuery(id+"F4.wireOp",EDGE,"E6.3.2.7")])],"isStart":false});
            var Q188;
            Q188=makeQuery(id+"F5.opExtrude","CAP_EDGE",EDGE,{"disambiguationData":[OSD([sQuery(id+"F4.wireOp",EDGE,"E6.4.2.1")])],"isStart":false});
            var Q189;
            Q189=makeQuery(id+"F5.opExtrude","CAP_EDGE",EDGE,{"disambiguationData":[OSD([sQuery(id+"F4.wireOp",EDGE,"E6.4.2.3")])],"isStart":false});
            var Q190;
            Q190=makeQuery(id+"F5.opExtrude","CAP_EDGE",EDGE,{"disambiguationData":[OSD([sQuery(id+"F4.wireOp",EDGE,"E6.4.2.5")])],"isStart":false});
            var Q191;
            Q191=makeQuery(id+"F5.opExtrude","CAP_EDGE",EDGE,{"disambiguationData":[OSD([sQuery(id+"F4.wireOp",EDGE,"E6.4.2.7")])],"isStart":false});
            var Q192;
            Q192=makeQuery(id+"F5.opExtrude","CAP_EDGE",EDGE,{"disambiguationData":[OSD([sQuery(id+"F4.wireOp",EDGE,"E7.3.5.2")])],"isStart":false});
            var Q193;
            Q193=makeQuery(id+"F5.opExtrude","CAP_EDGE",EDGE,{"disambiguationData":[OSD([sQuery(id+"F4.wireOp",EDGE,"E7.5.5.2")])],"isStart":false});
            var Q194;
            Q194=makeQuery(id+"F5.opExtrude","CAP_EDGE",EDGE,{"disambiguationData":[OSD([sQuery(id+"F4.wireOp",EDGE,"E7.8.5.2")])],"isStart":false});
            var Q195;
            Q195=makeQuery(id+"F5.opExtrude","CAP_EDGE",EDGE,{"disambiguationData":[OSD([sQuery(id+"F4.wireOp",EDGE,"E7.10.5.2")])],"isStart":false});
            var Q196;
            Q196=makeQuery(id+"F5.opExtrude","CAP_EDGE",EDGE,{"disambiguationData":[OSD([sQuery(id+"F4.wireOp",EDGE,"E7.13.5.2")])],"isStart":false});
            var Q197;
            Q197=makeQuery(id+"F5.opExtrude","CAP_EDGE",EDGE,{"disambiguationData":[OSD([sQuery(id+"F4.wireOp",EDGE,"E7.15.5.2")])],"isStart":false});
            var Q198;
            Q198=makeQuery(id+"F5.opExtrude","CAP_EDGE",EDGE,{"disambiguationData":[OSD([sQuery(id+"F4.wireOp",EDGE,"E7.18.5.2")])],"isStart":false});
            var Q199;
            Q199=makeQuery(id+"F5.opExtrude","CAP_EDGE",EDGE,{"disambiguationData":[OSD([sQuery(id+"F4.wireOp",EDGE,"E7.0.5.2")])],"isStart":false});
            var Q200;
            Q200=makeQuery(id+"F5.opExtrude","CAP_EDGE",EDGE,{"disambiguationData":[OSD([sQuery(id+"F4.wireOp",EDGE,"E7.3.6.2")])],"isStart":false});
            var Q201;
            Q201=makeQuery(id+"F5.opExtrude","CAP_EDGE",EDGE,{"disambiguationData":[OSD([sQuery(id+"F4.wireOp",EDGE,"E7.5.6.2")])],"isStart":false});
            var Q202;
            Q202=makeQuery(id+"F5.opExtrude","CAP_EDGE",EDGE,{"disambiguationData":[OSD([sQuery(id+"F4.wireOp",EDGE,"E7.8.6.2")])],"isStart":false});
            var Q203;
            Q203=makeQuery(id+"F5.opExtrude","CAP_EDGE",EDGE,{"disambiguationData":[OSD([sQuery(id+"F4.wireOp",EDGE,"E7.10.6.2")])],"isStart":false});
            var Q204;
            Q204=makeQuery(id+"F5.opExtrude","CAP_EDGE",EDGE,{"disambiguationData":[OSD([sQuery(id+"F4.wireOp",EDGE,"E7.13.6.2")])],"isStart":false});
            var Q205;
            Q205=makeQuery(id+"F5.opExtrude","CAP_EDGE",EDGE,{"disambiguationData":[OSD([sQuery(id+"F4.wireOp",EDGE,"E7.15.6.2")])],"isStart":false});
            var Q206;
            Q206=makeQuery(id+"F5.opExtrude","CAP_EDGE",EDGE,{"disambiguationData":[OSD([sQuery(id+"F4.wireOp",EDGE,"E7.18.6.2")])],"isStart":false});
            var Q207;
            Q207=makeQuery(id+"F5.opExtrude","CAP_EDGE",EDGE,{"disambiguationData":[OSD([sQuery(id+"F4.wireOp",EDGE,"E7.0.6.2")])],"isStart":false});
            var Q208;
            Q208=makeQuery(id+"F5.opExtrude","CAP_EDGE",EDGE,{"disambiguationData":[OSD([sQuery(id+"F4.wireOp",EDGE,"E6.0.3.1")])],"isStart":false});
            var Q209;
            Q209=makeQuery(id+"F5.opExtrude","CAP_EDGE",EDGE,{"disambiguationData":[OSD([sQuery(id+"F4.wireOp",EDGE,"E6.0.3.3")])],"isStart":false});
            var Q210;
            Q210=makeQuery(id+"F5.opExtrude","CAP_EDGE",EDGE,{"disambiguationData":[OSD([sQuery(id+"F4.wireOp",EDGE,"E6.0.3.5")])],"isStart":false});
            var Q211;
            Q211=makeQuery(id+"F5.opExtrude","CAP_EDGE",EDGE,{"disambiguationData":[OSD([sQuery(id+"F4.wireOp",EDGE,"E6.0.3.7")])],"isStart":false});
            var Q212;
            Q212=makeQuery(id+"F5.opExtrude","CAP_EDGE",EDGE,{"disambiguationData":[OSD([sQuery(id+"F4.wireOp",EDGE,"E6.1.3.1")])],"isStart":false});
            var Q213;
            Q213=makeQuery(id+"F5.opExtrude","CAP_EDGE",EDGE,{"disambiguationData":[OSD([sQuery(id+"F4.wireOp",EDGE,"E6.1.3.3")])],"isStart":false});
            var Q214;
            Q214=makeQuery(id+"F5.opExtrude","CAP_EDGE",EDGE,{"disambiguationData":[OSD([sQuery(id+"F4.wireOp",EDGE,"E6.1.3.5")])],"isStart":false});
            var Q215;
            Q215=makeQuery(id+"F5.opExtrude","CAP_EDGE",EDGE,{"disambiguationData":[OSD([sQuery(id+"F4.wireOp",EDGE,"E6.1.3.7")])],"isStart":false});
            var Q216;
            Q216=makeQuery(id+"F5.opExtrude","CAP_EDGE",EDGE,{"disambiguationData":[OSD([sQuery(id+"F4.wireOp",EDGE,"E6.2.3.1")])],"isStart":false});
            var Q217;
            Q217=makeQuery(id+"F5.opExtrude","CAP_EDGE",EDGE,{"disambiguationData":[OSD([sQuery(id+"F4.wireOp",EDGE,"E6.2.3.3")])],"isStart":false});
            var Q218;
            Q218=makeQuery(id+"F5.opExtrude","CAP_EDGE",EDGE,{"disambiguationData":[OSD([sQuery(id+"F4.wireOp",EDGE,"E6.2.3.5")])],"isStart":false});
            var Q219;
            Q219=makeQuery(id+"F5.opExtrude","CAP_EDGE",EDGE,{"disambiguationData":[OSD([sQuery(id+"F4.wireOp",EDGE,"E6.2.3.7")])],"isStart":false});
            var Q220;
            Q220=makeQuery(id+"F5.opExtrude","CAP_EDGE",EDGE,{"disambiguationData":[OSD([sQuery(id+"F4.wireOp",EDGE,"E6.3.3.1")])],"isStart":false});
            var Q221;
            Q221=makeQuery(id+"F5.opExtrude","CAP_EDGE",EDGE,{"disambiguationData":[OSD([sQuery(id+"F4.wireOp",EDGE,"E6.3.3.3")])],"isStart":false});
            var Q222;
            Q222=makeQuery(id+"F5.opExtrude","CAP_EDGE",EDGE,{"disambiguationData":[OSD([sQuery(id+"F4.wireOp",EDGE,"E6.3.3.5")])],"isStart":false});
            var Q223;
            Q223=makeQuery(id+"F5.opExtrude","CAP_EDGE",EDGE,{"disambiguationData":[OSD([sQuery(id+"F4.wireOp",EDGE,"E6.3.3.7")])],"isStart":false});
            var Q224;
            Q224=makeQuery(id+"F5.opExtrude","CAP_EDGE",EDGE,{"disambiguationData":[OSD([sQuery(id+"F4.wireOp",EDGE,"E6.4.3.1")])],"isStart":false});
            var Q225;
            Q225=makeQuery(id+"F5.opExtrude","CAP_EDGE",EDGE,{"disambiguationData":[OSD([sQuery(id+"F4.wireOp",EDGE,"E6.4.3.3")])],"isStart":false});
            var Q226;
            Q226=makeQuery(id+"F5.opExtrude","CAP_EDGE",EDGE,{"disambiguationData":[OSD([sQuery(id+"F4.wireOp",EDGE,"E6.4.3.5")])],"isStart":false});
            var Q227;
            Q227=makeQuery(id+"F5.opExtrude","CAP_EDGE",EDGE,{"disambiguationData":[OSD([sQuery(id+"F4.wireOp",EDGE,"E6.4.3.7")])],"isStart":false});
            var Q228;
            Q228=makeQuery(id+"F5.opExtrude","CAP_EDGE",EDGE,{"disambiguationData":[OSD([sQuery(id+"F4.wireOp",EDGE,"E7.3.5.3")])],"isStart":false});
            var Q229;
            Q229=makeQuery(id+"F5.opExtrude","CAP_EDGE",EDGE,{"disambiguationData":[OSD([sQuery(id+"F4.wireOp",EDGE,"E7.5.5.3")])],"isStart":false});
            var Q230;
            Q230=makeQuery(id+"F5.opExtrude","CAP_EDGE",EDGE,{"disambiguationData":[OSD([sQuery(id+"F4.wireOp",EDGE,"E7.8.5.3")])],"isStart":false});
            var Q231;
            Q231=makeQuery(id+"F5.opExtrude","CAP_EDGE",EDGE,{"disambiguationData":[OSD([sQuery(id+"F4.wireOp",EDGE,"E7.10.5.3")])],"isStart":false});
            var Q232;
            Q232=makeQuery(id+"F5.opExtrude","CAP_EDGE",EDGE,{"disambiguationData":[OSD([sQuery(id+"F4.wireOp",EDGE,"E7.13.5.3")])],"isStart":false});
            var Q233;
            Q233=makeQuery(id+"F5.opExtrude","CAP_EDGE",EDGE,{"disambiguationData":[OSD([sQuery(id+"F4.wireOp",EDGE,"E7.15.5.3")])],"isStart":false});
            var Q234;
            Q234=makeQuery(id+"F5.opExtrude","CAP_EDGE",EDGE,{"disambiguationData":[OSD([sQuery(id+"F4.wireOp",EDGE,"E7.18.5.3")])],"isStart":false});
            var Q235;
            Q235=makeQuery(id+"F5.opExtrude","CAP_EDGE",EDGE,{"disambiguationData":[OSD([sQuery(id+"F4.wireOp",EDGE,"E7.0.5.3")])],"isStart":false});
            var Q236;
            Q236=makeQuery(id+"F5.opExtrude","CAP_EDGE",EDGE,{"disambiguationData":[OSD([sQuery(id+"F4.wireOp",EDGE,"E7.3.6.3")])],"isStart":false});
            var Q237;
            Q237=makeQuery(id+"F5.opExtrude","CAP_EDGE",EDGE,{"disambiguationData":[OSD([sQuery(id+"F4.wireOp",EDGE,"E7.5.6.3")])],"isStart":false});
            var Q238;
            Q238=makeQuery(id+"F5.opExtrude","CAP_EDGE",EDGE,{"disambiguationData":[OSD([sQuery(id+"F4.wireOp",EDGE,"E7.8.6.3")])],"isStart":false});
            var Q239;
            Q239=makeQuery(id+"F5.opExtrude","CAP_EDGE",EDGE,{"disambiguationData":[OSD([sQuery(id+"F4.wireOp",EDGE,"E7.10.6.3")])],"isStart":false});
            var Q240;
            Q240=makeQuery(id+"F5.opExtrude","CAP_EDGE",EDGE,{"disambiguationData":[OSD([sQuery(id+"F4.wireOp",EDGE,"E7.13.6.3")])],"isStart":false});
            var Q241;
            Q241=makeQuery(id+"F5.opExtrude","CAP_EDGE",EDGE,{"disambiguationData":[OSD([sQuery(id+"F4.wireOp",EDGE,"E7.15.6.3")])],"isStart":false});
            var Q242;
            Q242=makeQuery(id+"F5.opExtrude","CAP_EDGE",EDGE,{"disambiguationData":[OSD([sQuery(id+"F4.wireOp",EDGE,"E7.18.6.3")])],"isStart":false});
            var Q243;
            Q243=makeQuery(id+"F5.opExtrude","CAP_EDGE",EDGE,{"disambiguationData":[OSD([sQuery(id+"F4.wireOp",EDGE,"E7.0.6.3")])],"isStart":false});
            var Q244;
            Q244=makeQuery(id+"F5.opExtrude","CAP_EDGE",EDGE,{"disambiguationData":[OSD([sQuery(id+"F4.wireOp",EDGE,"E6.0.4.1")])],"isStart":false});
            var Q245;
            Q245=makeQuery(id+"F5.opExtrude","CAP_EDGE",EDGE,{"disambiguationData":[OSD([sQuery(id+"F4.wireOp",EDGE,"E6.0.4.3")])],"isStart":false});
            var Q246;
            Q246=makeQuery(id+"F5.opExtrude","CAP_EDGE",EDGE,{"disambiguationData":[OSD([sQuery(id+"F4.wireOp",EDGE,"E6.0.4.5")])],"isStart":false});
            var Q247;
            Q247=makeQuery(id+"F5.opExtrude","CAP_EDGE",EDGE,{"disambiguationData":[OSD([sQuery(id+"F4.wireOp",EDGE,"E6.0.4.7")])],"isStart":false});
            var Q248;
            Q248=makeQuery(id+"F5.opExtrude","CAP_EDGE",EDGE,{"disambiguationData":[OSD([sQuery(id+"F4.wireOp",EDGE,"E6.1.4.1")])],"isStart":false});
            var Q249;
            Q249=makeQuery(id+"F5.opExtrude","CAP_EDGE",EDGE,{"disambiguationData":[OSD([sQuery(id+"F4.wireOp",EDGE,"E6.1.4.3")])],"isStart":false});
            var Q250;
            Q250=makeQuery(id+"F5.opExtrude","CAP_EDGE",EDGE,{"disambiguationData":[OSD([sQuery(id+"F4.wireOp",EDGE,"E6.1.4.5")])],"isStart":false});
            var Q251;
            Q251=makeQuery(id+"F5.opExtrude","CAP_EDGE",EDGE,{"disambiguationData":[OSD([sQuery(id+"F4.wireOp",EDGE,"E6.1.4.7")])],"isStart":false});
            var Q252;
            Q252=makeQuery(id+"F5.opExtrude","CAP_EDGE",EDGE,{"disambiguationData":[OSD([sQuery(id+"F4.wireOp",EDGE,"E6.2.4.1")])],"isStart":false});
            var Q253;
            Q253=makeQuery(id+"F5.opExtrude","CAP_EDGE",EDGE,{"disambiguationData":[OSD([sQuery(id+"F4.wireOp",EDGE,"E6.2.4.3")])],"isStart":false});
            var Q254;
            Q254=makeQuery(id+"F5.opExtrude","CAP_EDGE",EDGE,{"disambiguationData":[OSD([sQuery(id+"F4.wireOp",EDGE,"E6.2.4.5")])],"isStart":false});
            var Q255;
            Q255=makeQuery(id+"F5.opExtrude","CAP_EDGE",EDGE,{"disambiguationData":[OSD([sQuery(id+"F4.wireOp",EDGE,"E6.2.4.7")])],"isStart":false});
            var Q256;
            Q256=makeQuery(id+"F5.opExtrude","CAP_EDGE",EDGE,{"disambiguationData":[OSD([sQuery(id+"F4.wireOp",EDGE,"E6.3.4.1")])],"isStart":false});
            var Q257;
            Q257=makeQuery(id+"F5.opExtrude","CAP_EDGE",EDGE,{"disambiguationData":[OSD([sQuery(id+"F4.wireOp",EDGE,"E6.3.4.3")])],"isStart":false});
            var Q258;
            Q258=makeQuery(id+"F5.opExtrude","CAP_EDGE",EDGE,{"disambiguationData":[OSD([sQuery(id+"F4.wireOp",EDGE,"E6.3.4.5")])],"isStart":false});
            var Q259;
            Q259=makeQuery(id+"F5.opExtrude","CAP_EDGE",EDGE,{"disambiguationData":[OSD([sQuery(id+"F4.wireOp",EDGE,"E6.3.4.7")])],"isStart":false});
            var Q260;
            Q260=makeQuery(id+"F5.opExtrude","CAP_EDGE",EDGE,{"disambiguationData":[OSD([sQuery(id+"F4.wireOp",EDGE,"E6.4.4.1")])],"isStart":false});
            var Q261;
            Q261=makeQuery(id+"F5.opExtrude","CAP_EDGE",EDGE,{"disambiguationData":[OSD([sQuery(id+"F4.wireOp",EDGE,"E6.4.4.3")])],"isStart":false});
            var Q262;
            Q262=makeQuery(id+"F5.opExtrude","CAP_EDGE",EDGE,{"disambiguationData":[OSD([sQuery(id+"F4.wireOp",EDGE,"E6.4.4.5")])],"isStart":false});
            var Q263;
            Q263=makeQuery(id+"F5.opExtrude","CAP_EDGE",EDGE,{"disambiguationData":[OSD([sQuery(id+"F4.wireOp",EDGE,"E6.4.4.7")])],"isStart":false});
            var Q264;
            Q264=makeQuery(id+"F5.opExtrude","CAP_EDGE",EDGE,{"disambiguationData":[OSD([sQuery(id+"F4.wireOp",EDGE,"E7.3.5.4")])],"isStart":false});
            var Q265;
            Q265=makeQuery(id+"F5.opExtrude","CAP_EDGE",EDGE,{"disambiguationData":[OSD([sQuery(id+"F4.wireOp",EDGE,"E7.5.5.4")])],"isStart":false});
            var Q266;
            Q266=makeQuery(id+"F5.opExtrude","CAP_EDGE",EDGE,{"disambiguationData":[OSD([sQuery(id+"F4.wireOp",EDGE,"E7.8.5.4")])],"isStart":false});
            var Q267;
            Q267=makeQuery(id+"F5.opExtrude","CAP_EDGE",EDGE,{"disambiguationData":[OSD([sQuery(id+"F4.wireOp",EDGE,"E7.10.5.4")])],"isStart":false});
            var Q268;
            Q268=makeQuery(id+"F5.opExtrude","CAP_EDGE",EDGE,{"disambiguationData":[OSD([sQuery(id+"F4.wireOp",EDGE,"E7.13.5.4")])],"isStart":false});
            var Q269;
            Q269=makeQuery(id+"F5.opExtrude","CAP_EDGE",EDGE,{"disambiguationData":[OSD([sQuery(id+"F4.wireOp",EDGE,"E7.15.5.4")])],"isStart":false});
            var Q270;
            Q270=makeQuery(id+"F5.opExtrude","CAP_EDGE",EDGE,{"disambiguationData":[OSD([sQuery(id+"F4.wireOp",EDGE,"E7.18.5.4")])],"isStart":false});
            var Q271;
            Q271=makeQuery(id+"F5.opExtrude","CAP_EDGE",EDGE,{"disambiguationData":[OSD([sQuery(id+"F4.wireOp",EDGE,"E7.0.5.4")])],"isStart":false});
            var Q272;
            Q272=makeQuery(id+"F5.opExtrude","CAP_EDGE",EDGE,{"disambiguationData":[OSD([sQuery(id+"F4.wireOp",EDGE,"E7.3.6.4")])],"isStart":false});
            var Q273;
            Q273=makeQuery(id+"F5.opExtrude","CAP_EDGE",EDGE,{"disambiguationData":[OSD([sQuery(id+"F4.wireOp",EDGE,"E7.5.6.4")])],"isStart":false});
            var Q274;
            Q274=makeQuery(id+"F5.opExtrude","CAP_EDGE",EDGE,{"disambiguationData":[OSD([sQuery(id+"F4.wireOp",EDGE,"E7.8.6.4")])],"isStart":false});
            var Q275;
            Q275=makeQuery(id+"F5.opExtrude","CAP_EDGE",EDGE,{"disambiguationData":[OSD([sQuery(id+"F4.wireOp",EDGE,"E7.10.6.4")])],"isStart":false});
            var Q276;
            Q276=makeQuery(id+"F5.opExtrude","CAP_EDGE",EDGE,{"disambiguationData":[OSD([sQuery(id+"F4.wireOp",EDGE,"E7.13.6.4")])],"isStart":false});
            var Q277;
            Q277=makeQuery(id+"F5.opExtrude","CAP_EDGE",EDGE,{"disambiguationData":[OSD([sQuery(id+"F4.wireOp",EDGE,"E7.15.6.4")])],"isStart":false});
            var Q278;
            Q278=makeQuery(id+"F5.opExtrude","CAP_EDGE",EDGE,{"disambiguationData":[OSD([sQuery(id+"F4.wireOp",EDGE,"E7.18.6.4")])],"isStart":false});
            var Q279;
            Q279=makeQuery(id+"F5.opExtrude","CAP_EDGE",EDGE,{"disambiguationData":[OSD([sQuery(id+"F4.wireOp",EDGE,"E7.0.6.4")])],"isStart":false});
            var Q280;
            Q280=makeQuery(id+"F5.opExtrude","CAP_EDGE",EDGE,{"disambiguationData":[OSD([sQuery(id+"F4.wireOp",EDGE,"E8.0.0.5")])],"isStart":false});
            var Q281;
            Q281=makeQuery(id+"F5.opExtrude","CAP_EDGE",EDGE,{"disambiguationData":[OSD([sQuery(id+"F4.wireOp",EDGE,"E8.3.0.5")])],"isStart":false});
            var Q282;
            Q282=makeQuery(id+"F5.opExtrude","CAP_EDGE",EDGE,{"disambiguationData":[OSD([sQuery(id+"F4.wireOp",EDGE,"E8.5.0.5")])],"isStart":false});
            var Q283;
            Q283=makeQuery(id+"F5.opExtrude","CAP_EDGE",EDGE,{"disambiguationData":[OSD([sQuery(id+"F4.wireOp",EDGE,"E8.8.0.5")])],"isStart":false});
            var Q284;
            Q284=makeQuery(id+"F5.opExtrude","CAP_EDGE",EDGE,{"disambiguationData":[OSD([sQuery(id+"F4.wireOp",EDGE,"E8.10.0.5")])],"isStart":false});
            var Q285;
            Q285=makeQuery(id+"F5.opExtrude","CAP_EDGE",EDGE,{"disambiguationData":[OSD([sQuery(id+"F4.wireOp",EDGE,"E8.13.0.5")])],"isStart":false});
            var Q286;
            Q286=makeQuery(id+"F5.opExtrude","CAP_EDGE",EDGE,{"disambiguationData":[OSD([sQuery(id+"F4.wireOp",EDGE,"E8.15.0.5")])],"isStart":false});
            var Q287;
            Q287=makeQuery(id+"F5.opExtrude","CAP_EDGE",EDGE,{"disambiguationData":[OSD([sQuery(id+"F4.wireOp",EDGE,"E8.18.0.5")])],"isStart":false});
            var Q288;
            Q288=makeQuery(id+"F5.opExtrude","CAP_EDGE",EDGE,{"disambiguationData":[OSD([sQuery(id+"F4.wireOp",EDGE,"E8.0.1.5")])],"isStart":false});
            var Q289;
            Q289=makeQuery(id+"F5.opExtrude","CAP_EDGE",EDGE,{"disambiguationData":[OSD([sQuery(id+"F4.wireOp",EDGE,"E8.3.1.5")])],"isStart":false});
            var Q290;
            Q290=makeQuery(id+"F5.opExtrude","CAP_EDGE",EDGE,{"disambiguationData":[OSD([sQuery(id+"F4.wireOp",EDGE,"E8.5.1.5")])],"isStart":false});
            var Q291;
            Q291=makeQuery(id+"F5.opExtrude","CAP_EDGE",EDGE,{"disambiguationData":[OSD([sQuery(id+"F4.wireOp",EDGE,"E8.8.1.5")])],"isStart":false});
            var Q292;
            Q292=makeQuery(id+"F5.opExtrude","CAP_EDGE",EDGE,{"disambiguationData":[OSD([sQuery(id+"F4.wireOp",EDGE,"E8.10.1.5")])],"isStart":false});
            var Q293;
            Q293=makeQuery(id+"F5.opExtrude","CAP_EDGE",EDGE,{"disambiguationData":[OSD([sQuery(id+"F4.wireOp",EDGE,"E8.13.1.5")])],"isStart":false});
            var Q294;
            Q294=makeQuery(id+"F5.opExtrude","CAP_EDGE",EDGE,{"disambiguationData":[OSD([sQuery(id+"F4.wireOp",EDGE,"E8.15.1.5")])],"isStart":false});
            var Q295;
            Q295=makeQuery(id+"F5.opExtrude","CAP_EDGE",EDGE,{"disambiguationData":[OSD([sQuery(id+"F4.wireOp",EDGE,"E8.18.1.5")])],"isStart":false});
            var Q296;
            Q296=makeQuery(id+"F5.opExtrude","CAP_EDGE",EDGE,{"disambiguationData":[OSD([sQuery(id+"F4.wireOp",EDGE,"E8.3.2.5")])],"isStart":false});
            var Q297;
            Q297=makeQuery(id+"F5.opExtrude","CAP_EDGE",EDGE,{"disambiguationData":[OSD([sQuery(id+"F4.wireOp",EDGE,"E8.5.2.5")])],"isStart":false});
            var Q298;
            Q298=makeQuery(id+"F5.opExtrude","CAP_EDGE",EDGE,{"disambiguationData":[OSD([sQuery(id+"F4.wireOp",EDGE,"E8.8.2.5")])],"isStart":false});
            var Q299;
            Q299=makeQuery(id+"F5.opExtrude","CAP_EDGE",EDGE,{"disambiguationData":[OSD([sQuery(id+"F4.wireOp",EDGE,"E8.10.2.5")])],"isStart":false});
            var Q300;
            Q300=makeQuery(id+"F5.opExtrude","CAP_EDGE",EDGE,{"disambiguationData":[OSD([sQuery(id+"F4.wireOp",EDGE,"E8.13.2.5")])],"isStart":false});
            var Q301;
            Q301=makeQuery(id+"F5.opExtrude","CAP_EDGE",EDGE,{"disambiguationData":[OSD([sQuery(id+"F4.wireOp",EDGE,"E8.15.2.5")])],"isStart":false});
            var Q302;
            Q302=makeQuery(id+"F5.opExtrude","CAP_EDGE",EDGE,{"disambiguationData":[OSD([sQuery(id+"F4.wireOp",EDGE,"E8.18.2.5")])],"isStart":false});
            var Q303;
            Q303=makeQuery(id+"F5.opExtrude","CAP_EDGE",EDGE,{"disambiguationData":[OSD([sQuery(id+"F4.wireOp",EDGE,"E8.0.2.5")])],"isStart":false});
            var Q304;
            Q304=makeQuery(id+"F5.opExtrude","CAP_EDGE",EDGE,{"disambiguationData":[OSD([sQuery(id+"F4.wireOp",EDGE,"E8.0.3.5")])],"isStart":false});
            var Q305;
            Q305=makeQuery(id+"F5.opExtrude","CAP_EDGE",EDGE,{"disambiguationData":[OSD([sQuery(id+"F4.wireOp",EDGE,"E8.3.3.5")])],"isStart":false});
            var Q306;
            Q306=makeQuery(id+"F5.opExtrude","CAP_EDGE",EDGE,{"disambiguationData":[OSD([sQuery(id+"F4.wireOp",EDGE,"E8.5.3.5")])],"isStart":false});
            var Q307;
            Q307=makeQuery(id+"F5.opExtrude","CAP_EDGE",EDGE,{"disambiguationData":[OSD([sQuery(id+"F4.wireOp",EDGE,"E8.8.3.5")])],"isStart":false});
            var Q308;
            Q308=makeQuery(id+"F5.opExtrude","CAP_EDGE",EDGE,{"disambiguationData":[OSD([sQuery(id+"F4.wireOp",EDGE,"E8.10.3.5")])],"isStart":false});
            var Q309;
            Q309=makeQuery(id+"F5.opExtrude","CAP_EDGE",EDGE,{"disambiguationData":[OSD([sQuery(id+"F4.wireOp",EDGE,"E8.13.3.5")])],"isStart":false});
            var Q310;
            Q310=makeQuery(id+"F5.opExtrude","CAP_EDGE",EDGE,{"disambiguationData":[OSD([sQuery(id+"F4.wireOp",EDGE,"E8.15.3.5")])],"isStart":false});
            var Q311;
            Q311=makeQuery(id+"F5.opExtrude","CAP_EDGE",EDGE,{"disambiguationData":[OSD([sQuery(id+"F4.wireOp",EDGE,"E8.18.3.5")])],"isStart":false});
            var Q312;
            Q312=makeQuery(id+"F5.opExtrude","CAP_EDGE",EDGE,{"disambiguationData":[OSD([sQuery(id+"F4.wireOp",EDGE,"E8.0.4.5")])],"isStart":false});
            var Q313;
            Q313=makeQuery(id+"F5.opExtrude","CAP_EDGE",EDGE,{"disambiguationData":[OSD([sQuery(id+"F4.wireOp",EDGE,"E8.3.4.5")])],"isStart":false});
            var Q314;
            Q314=makeQuery(id+"F5.opExtrude","CAP_EDGE",EDGE,{"disambiguationData":[OSD([sQuery(id+"F4.wireOp",EDGE,"E8.5.4.5")])],"isStart":false});
            var Q315;
            Q315=makeQuery(id+"F5.opExtrude","CAP_EDGE",EDGE,{"disambiguationData":[OSD([sQuery(id+"F4.wireOp",EDGE,"E8.8.4.5")])],"isStart":false});
            var Q316;
            Q316=makeQuery(id+"F5.opExtrude","CAP_EDGE",EDGE,{"disambiguationData":[OSD([sQuery(id+"F4.wireOp",EDGE,"E8.10.4.5")])],"isStart":false});
            var Q317;
            Q317=makeQuery(id+"F5.opExtrude","CAP_EDGE",EDGE,{"disambiguationData":[OSD([sQuery(id+"F4.wireOp",EDGE,"E8.13.4.5")])],"isStart":false});
            var Q318;
            Q318=makeQuery(id+"F5.opExtrude","CAP_EDGE",EDGE,{"disambiguationData":[OSD([sQuery(id+"F4.wireOp",EDGE,"E8.15.4.5")])],"isStart":false});
            var Q319;
            Q319=makeQuery(id+"F5.opExtrude","CAP_EDGE",EDGE,{"disambiguationData":[OSD([sQuery(id+"F4.wireOp",EDGE,"E8.18.4.5")])],"isStart":false});
            var Q320;
            Q320=makeQuery(id+"F5.opExtrude","CAP_EDGE",EDGE,{"disambiguationData":[OSD([sQuery(id+"F4.wireOp",EDGE,"E8.0.5.5")])],"isStart":false});
            var Q321;
            Q321=makeQuery(id+"F5.opExtrude","CAP_EDGE",EDGE,{"disambiguationData":[OSD([sQuery(id+"F4.wireOp",EDGE,"E8.3.5.5")])],"isStart":false});
            var Q322;
            Q322=makeQuery(id+"F5.opExtrude","CAP_EDGE",EDGE,{"disambiguationData":[OSD([sQuery(id+"F4.wireOp",EDGE,"E8.5.5.5")])],"isStart":false});
            var Q323;
            Q323=makeQuery(id+"F5.opExtrude","CAP_EDGE",EDGE,{"disambiguationData":[OSD([sQuery(id+"F4.wireOp",EDGE,"E8.8.5.5")])],"isStart":false});
            var Q324;
            Q324=makeQuery(id+"F5.opExtrude","CAP_EDGE",EDGE,{"disambiguationData":[OSD([sQuery(id+"F4.wireOp",EDGE,"E8.10.5.5")])],"isStart":false});
            var Q325;
            Q325=makeQuery(id+"F5.opExtrude","CAP_EDGE",EDGE,{"disambiguationData":[OSD([sQuery(id+"F4.wireOp",EDGE,"E8.13.5.5")])],"isStart":false});
            var Q326;
            Q326=makeQuery(id+"F5.opExtrude","CAP_EDGE",EDGE,{"disambiguationData":[OSD([sQuery(id+"F4.wireOp",EDGE,"E8.15.5.5")])],"isStart":false});
            var Q327;
            Q327=makeQuery(id+"F5.opExtrude","CAP_EDGE",EDGE,{"disambiguationData":[OSD([sQuery(id+"F4.wireOp",EDGE,"E8.18.5.5")])],"isStart":false});
            var Q328;
            Q328=makeQuery(id+"F5.opExtrude","CAP_EDGE",EDGE,{"disambiguationData":[OSD([sQuery(id+"F4.wireOp",EDGE,"E8.0.6.5")])],"isStart":false});
            var Q329;
            Q329=makeQuery(id+"F5.opExtrude","CAP_EDGE",EDGE,{"disambiguationData":[OSD([sQuery(id+"F4.wireOp",EDGE,"E8.3.6.5")])],"isStart":false});
            var Q330;
            Q330=makeQuery(id+"F5.opExtrude","CAP_EDGE",EDGE,{"disambiguationData":[OSD([sQuery(id+"F4.wireOp",EDGE,"E8.5.6.5")])],"isStart":false});
            var Q331;
            Q331=makeQuery(id+"F5.opExtrude","CAP_EDGE",EDGE,{"disambiguationData":[OSD([sQuery(id+"F4.wireOp",EDGE,"E8.8.6.5")])],"isStart":false});
            var Q332;
            Q332=makeQuery(id+"F5.opExtrude","CAP_EDGE",EDGE,{"disambiguationData":[OSD([sQuery(id+"F4.wireOp",EDGE,"E8.10.6.5")])],"isStart":false});
            var Q333;
            Q333=makeQuery(id+"F5.opExtrude","CAP_EDGE",EDGE,{"disambiguationData":[OSD([sQuery(id+"F4.wireOp",EDGE,"E8.13.6.5")])],"isStart":false});
            var Q334;
            Q334=makeQuery(id+"F5.opExtrude","CAP_EDGE",EDGE,{"disambiguationData":[OSD([sQuery(id+"F4.wireOp",EDGE,"E8.15.6.5")])],"isStart":false});
            var Q335;
            Q335=makeQuery(id+"F5.opExtrude","CAP_EDGE",EDGE,{"disambiguationData":[OSD([sQuery(id+"F4.wireOp",EDGE,"E8.18.6.5")])],"isStart":false});
            chamfer(context, id + "F8", {"entities" : qUnion([Q0, Q1, Q2, Q3, Q4, Q5, Q6, Q7, Q8, Q9, Q10, Q11, Q12, Q13, Q14, Q15, Q16, Q17, Q18, Q19, Q20, Q21, Q22, Q23, Q24, Q25, Q26, Q27, Q28, Q29, Q30, Q31, Q32, Q33, Q34, Q35, Q36, Q37, Q38, Q39, Q40, Q41, Q42, Q43, Q44, Q45, Q46, Q47, Q48, Q49, Q50, Q51, Q52, Q53, Q54, Q55, Q56, Q57, Q58, Q59, Q60, Q61, Q62, Q63, Q64, Q65, Q66, Q67, Q68, Q69, Q70, Q71, Q72, Q73, Q74, Q75, Q76, Q77, Q78, Q79, Q80, Q81, Q82, Q83, Q84, Q85, Q86, Q87, Q88, Q89, Q90, Q91, Q92, Q93, Q94, Q95, Q96, Q97, Q98, Q99, Q100, Q101, Q102, Q103, Q104, Q105, Q106, Q107, Q108, Q109, Q110, Q111, Q112, Q113, Q114, Q115, Q116, Q117, Q118, Q119, Q120, Q121, Q122, Q123, Q124, Q125, Q126, Q127, Q128, Q129, Q130, Q131, Q132, Q133, Q134, Q135, Q136, Q137, Q138, Q139, Q140, Q141, Q142, Q143, Q144, Q145, Q146, Q147, Q148, Q149, Q150, Q151, Q152, Q153, Q154, Q155, Q156, Q157, Q158, Q159, Q160, Q161, Q162, Q163, Q164, Q165, Q166, Q167, Q168, Q169, Q170, Q171, Q172, Q173, Q174, Q175, Q176, Q177, Q178, Q179, Q180, Q181, Q182, Q183, Q184, Q185, Q186, Q187, Q188, Q189, Q190, Q191, Q192, Q193, Q194, Q195, Q196, Q197, Q198, Q199, Q200, Q201, Q202, Q203, Q204, Q205, Q206, Q207, Q208, Q209, Q210, Q211, Q212, Q213, Q214, Q215, Q216, Q217, Q218, Q219, Q220, Q221, Q222, Q223, Q224, Q225, Q226, Q227, Q228, Q229, Q230, Q231, Q232, Q233, Q234, Q235, Q236, Q237, Q238, Q239, Q240, Q241, Q242, Q243, Q244, Q245, Q246, Q247, Q248, Q249, Q250, Q251, Q252, Q253, Q254, Q255, Q256, Q257, Q258, Q259, Q260, Q261, Q262, Q263, Q264, Q265, Q266, Q267, Q268, Q269, Q270, Q271, Q272, Q273, Q274, Q275, Q276, Q277, Q278, Q279, Q280, Q281, Q282, Q283, Q284, Q285, Q286, Q287, Q288, Q289, Q290, Q291, Q292, Q293, Q294, Q295, Q296, Q297, Q298, Q299, Q300, Q301, Q302, Q303, Q304, Q305, Q306, Q307, Q308, Q309, Q310, Q311, Q312, Q313, Q314, Q315, Q316, Q317, Q318, Q319, Q320, Q321, Q322, Q323, Q324, Q325, Q326, Q327, Q328, Q329, Q330, Q331, Q332, Q333, Q334, Q335]), "chamferType" : ChamferType.OFFSET_ANGLE, "width" : .5 * mm, "oppositeDirection" : false, "angle" : 75 * degree, "tangentPropagation" : true});
        }
        {
            var Q0;
            Q0=makeQuery(id+"F5.opExtrude","CAP_EDGE",EDGE,{"disambiguationData":[OSD([sQuery(id+"F0.wireOp",EDGE,"E0.left")])],"isStart":false});
            var Q1;
            Q1=makeQuery(id+"F5.opExtrude","CAP_EDGE",EDGE,{"disambiguationData":[OSD([sQuery(id+"F0.wireOp",EDGE,"E0.bottom")])],"isStart":false});
            var Q2;
            Q2=makeQuery(id+"F5.opExtrude","CAP_EDGE",EDGE,{"disambiguationData":[OSD([sQuery(id+"F0.wireOp",EDGE,"E0.right")])],"isStart":false});
            var Q3;
            {var subQ0=sQuery(id+"F0.wireOp",EDGE,"E0.right");var subQ1=sQuery(id+"F0.wireOp",EDGE,"E0.left");var subQ2=sQuery(id+"F0.wireOp",EDGE,"E0.top");var subQ3=sQuery(id+"F0.wireOp",EDGE,"E0.bottom");Q3=makeQuery(id+"F5.opExtrude","CAP_EDGE",EDGE,{"disambiguationData":[OSD([subQ3,subQ2,subQ1,subQ0]),TDD([makeQuery(id+"F4.imprint","IMPRINT",EDGE,{"derivedFrom":makeQuery(id+"F3.opFillet","BLEND_EDGE",EDGE,{"blendedFrom":[makeQuery(id+"F1.opExtrude","SWEPT_EDGE",EDGE,{"disambiguationData":[OSD([subQ3,subQ0])]}),makeQuery(id+"F1.opExtrude","CAP_FACE",FACE,{"disambiguationData":[OSD([subQ3,subQ2,subQ1,subQ0])],"isStart":false})],"blendedInto":[makeQuery(id+"F1.opExtrude","CAP_FACE",FACE,{"disambiguationData":[OSD([subQ3,subQ2,subQ1,subQ0])],"isStart":false})]})})])],"isStart":false});}
            var Q4;
            {var subQ0=sQuery(id+"F0.wireOp",EDGE,"E0.right");var subQ1=sQuery(id+"F0.wireOp",EDGE,"E0.left");var subQ2=sQuery(id+"F0.wireOp",EDGE,"E0.top");var subQ3=sQuery(id+"F0.wireOp",EDGE,"E0.bottom");Q4=makeQuery(id+"F5.opExtrude","CAP_EDGE",EDGE,{"disambiguationData":[OSD([subQ3,subQ2,subQ1,subQ0]),TDD([makeQuery(id+"F4.imprint","IMPRINT",EDGE,{"derivedFrom":makeQuery(id+"F2.opChamfer","BLEND_EDGE",EDGE,{"blendedFrom":[makeQuery(id+"F1.opExtrude","SWEPT_EDGE",EDGE,{"disambiguationData":[OSD([subQ3,subQ1])]}),makeQuery(id+"F1.opExtrude","CAP_FACE",FACE,{"disambiguationData":[OSD([subQ3,subQ2,subQ1,subQ0])],"isStart":false})],"blendedInto":[makeQuery(id+"F1.opExtrude","CAP_FACE",FACE,{"disambiguationData":[OSD([subQ3,subQ2,subQ1,subQ0])],"isStart":false})]})})])],"isStart":false});}
            chamfer(context, id + "F9", {"entities" : qUnion([Q0, Q1, Q2, Q3, Q4]), "chamferType" : ChamferType.OFFSET_ANGLE, "width" : 2 * mm, "oppositeDirection" : false, "angle" : 45 * degree, "tangentPropagation" : true});
        }
    });
